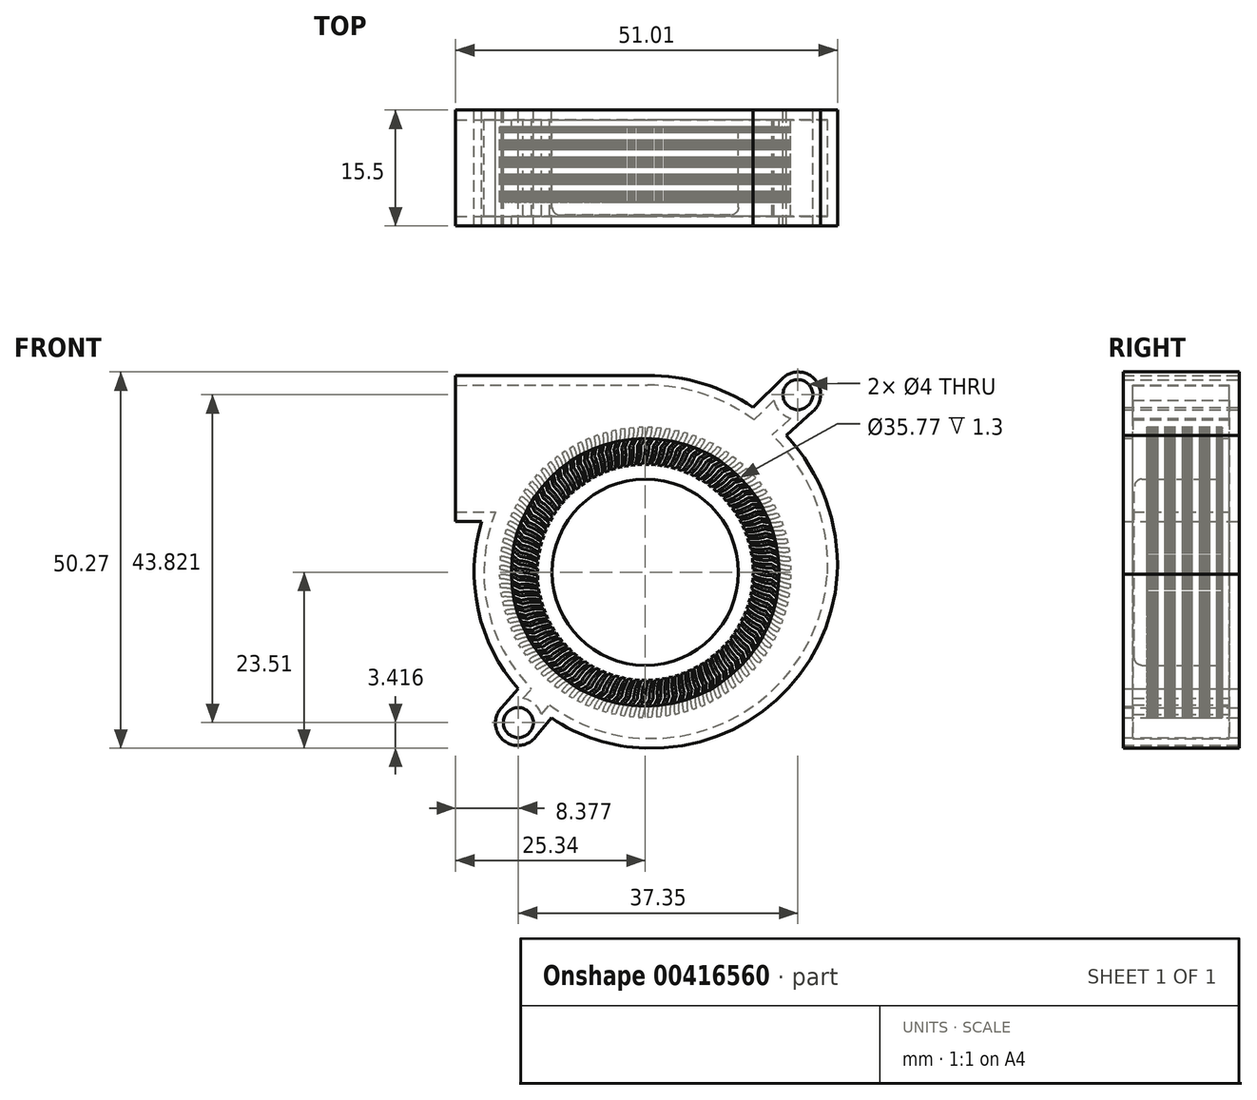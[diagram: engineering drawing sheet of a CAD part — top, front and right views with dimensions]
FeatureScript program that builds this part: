
annotation { "Feature Type Name" : "Feature", "Feature Type Description" : "" }
export const myFeature = defineFeature(function(context is Context, id is Id, definition is map)
    precondition{}
    {
        {
            var Q0;
            Q0=qCreatedBy(makeId("Front.planeOp"),FACE);
            var sketch = newSketch(context, id + "F0", { "sketchPlane" : qUnion([Q0])});
            skCircle(sketch, "E0", {"center": v(0, 0) * mm, "radius": 12.44 * mm});
            skCircle(sketch, "E1", {"center": v(0, 0) * mm, "radius": 15.98 * mm});
            skCircle(sketch, "E2.0", {"center": v(0, 0) * mm, "radius": 17.88 * mm});
            skLineSegment(sketch, "E3", {"start": v(-25.34, 6.78) * mm, "end": v(-25.34, 26.28) * mm});
            skLineSegment(sketch, "E4", {"start": v(-25.34, 6.78) * mm, "end": v(-21.86, 6.78) * mm});
            skLineSegment(sketch, "E5", {"start": v(-25.34, 26.28) * mm, "end": v(0.29, 26.3) * mm});
            skArc(sketch, "E6", {"start": v(25.64, -0.28) * mm, "mid": v(18.67, 18.45) * mm, "end": v(0.29, 26.3) * mm});
            skArc(sketch, "E7", {"start": v(0, -23.5) * mm, "mid": v(17.52, -17.08) * mm, "end": v(25.64, -0.28) * mm});
            skArc(sketch, "E8", {"start": v(-21.86, 6.78) * mm, "mid": v(-18.42, -13.77) * mm, "end": v(0, -23.5) * mm});
            skCircle(sketch, "E9", {"center": v(20.39, 23.73) * mm, "radius": 2 * mm});
            skCircle(sketch, "E10", {"center": v(-16.96, -20.1) * mm, "radius": 2 * mm});
            skLineSegment(sketch, "E11", {"start": v(22.42, 21.52) * mm, "end": v(18.83, 18.28) * mm});
            skLineSegment(sketch, "E12", {"start": v(18.32, 25.9) * mm, "end": v(14.4, 22.03) * mm});
            skArc(sketch, "E13", {"start": v(22.42, 21.52) * mm, "mid": v(22.61, 25.82) * mm, "end": v(18.32, 25.9) * mm});
            skLineSegment(sketch, "E14", {"start": v(-19.2, -18.1) * mm, "end": v(-16.96, -15.6) * mm});
            skLineSegment(sketch, "E15", {"start": v(-14.7, -22.06) * mm, "end": v(-12.56, -19.47) * mm});
            skArc(sketch, "E16", {"start": v(-19.2, -18.1) * mm, "mid": v(-19, -22.4) * mm, "end": v(-14.7, -22.06) * mm});
            skSolve(sketch);
        }
        {
            var Q0;
            Q0=makeQuery(id+"F0.imprint","IMPRINT",FACE,{"disambiguationData":[TD([[makeQuery(id+"F0.imprint","IMPRINT",EDGE,{"derivedFrom":sQuery(id+"F0.wireOp",EDGE,"E2.0")}),-1.0]])]});
            var Q1;
            Q1=makeQuery(id+"F0.imprint","IMPRINT",FACE,{"disambiguationData":[TD([[makeQuery(id+"F0.imprint","IMPRINT",EDGE,{"derivedFrom":sQuery(id+"F0.wireOp",EDGE,"E9")}),-1.0]])]});
            var Q2;
            Q2=makeQuery(id+"F0.imprint","IMPRINT",FACE,{"disambiguationData":[TD([[makeQuery(id+"F0.imprint","IMPRINT",EDGE,{"derivedFrom":sQuery(id+"F0.wireOp",EDGE,"E10")}),-1.0]])]});
            extrude(context, id + "F1", {"entities" : qUnion([Q0, Q1, Q2]), "depth" : 15.5 * mm});
        }
        {
            var Q0;
            Q0=makeQuery(id+"F1.opExtrude","SWEPT_FACE",FACE,{"disambiguationData":[OSD([sQuery(id+"F0.wireOp",EDGE,"E3")])]});
            var Q1;
            Q1=makeQuery(id+"F1.opExtrude","SWEPT_FACE",FACE,{"disambiguationData":[OSD([sQuery(id+"F0.wireOp",EDGE,"E2.0")])]});
            shell(context, id + "F2", {"entities" : qUnion([Q0, Q1]), "thickness" : 1.3 * mm});
        }
        {
            var Q0;
            Q0=makeQuery(id+"F0.imprint","IMPRINT",FACE,{"disambiguationData":[TD([[makeQuery(id+"F0.imprint","IMPRINT",EDGE,{"derivedFrom":sQuery(id+"F0.wireOp",EDGE,"E0")}),-1.0]])]});
            var Q1;
            Q1=makeQuery(id+"F0.imprint","IMPRINT",FACE,{"disambiguationData":[TD([[makeQuery(id+"F0.imprint","IMPRINT",EDGE,{"derivedFrom":sQuery(id+"F0.wireOp",EDGE,"E0")}),1.0]])]});
            extrude(context, id + "F3", {"entities" : qUnion([Q0, Q1]), "operationType" : NewBodyOperationType.ADD, "depth" : 1.3 * mm});
        }
        {
            var Q0;
            Q0=makeQuery(id+"F0.imprint","IMPRINT",FACE,{"disambiguationData":[TD([[makeQuery(id+"F0.imprint","IMPRINT",EDGE,{"derivedFrom":sQuery(id+"F0.wireOp",EDGE,"E1")}),-1.0]])]});
            var Q1;
            Q1=makeQuery(id+"F0.imprint","IMPRINT",FACE,{"disambiguationData":[TD([[makeQuery(id+"F0.imprint","IMPRINT",EDGE,{"derivedFrom":sQuery(id+"F0.wireOp",EDGE,"E0")}),-1.0]])]});
            var Q2;
            Q2=makeQuery(id+"F0.imprint","IMPRINT",FACE,{"disambiguationData":[TD([[makeQuery(id+"F0.imprint","IMPRINT",EDGE,{"derivedFrom":sQuery(id+"F0.wireOp",EDGE,"E0")}),1.0]])]});
            extrude(context, id + "F4", {"entities" : qUnion([Q0, Q1, Q2]), "depth" : 2.3 * mm});
        }
        {
            var Q0;
            Q0=makeQuery(id+"F0.imprint","IMPRINT",FACE,{"disambiguationData":[TD([[makeQuery(id+"F0.imprint","IMPRINT",EDGE,{"derivedFrom":sQuery(id+"F0.wireOp",EDGE,"E0")}),1.0]])]});
            extrude(context, id + "F5", {"entities" : qUnion([Q0]), "operationType" : NewBodyOperationType.ADD, "depth" : 14 * mm});
        }
        {
            var Q0;
            Q0=makeQuery(id+"F5.opExtrude","CAP_FACE",FACE,{"disambiguationData":[OSD([sQuery(id+"F0.wireOp",EDGE,"E0")])],"isStart":false});
            fillet(context, id + "F6", {"entities" : qUnion([Q0]), "radius" : 1 * mm, "tangentPropagation" : true, "allowEdgeOverflow" : false});
        }
        {
            var Q0;
            Q0=makeQuery(id+"F0.imprint","IMPRINT",FACE,{"disambiguationData":[TD([[makeQuery(id+"F0.imprint","IMPRINT",EDGE,{"derivedFrom":sQuery(id+"F0.wireOp",EDGE,"E1")}),-1.0]])]});
            extrude(context, id + "F7", {"entities" : qUnion([Q0]), "operationType" : NewBodyOperationType.ADD, "depth" : 1.3 * mm});
        }
        {
            var Q0;
            Q0=makeQuery(id+"F4.opExtrude","CAP_FACE",FACE,{"disambiguationData":[OSD([sQuery(id+"F0.wireOp",EDGE,"E2.0")])],"isStart":false});
            var sketch = newSketch(context, id + "F8", { "sketchPlane" : qUnion([Q0])});
            skLineSegment(sketch, "E17", {"start": v(-0.45, 14.4) * mm, "end": v(-1.01, 14.4) * mm});
            skLineSegment(sketch, "E18.MirrorCS", {"start": v(0.34, 19.42) * mm, "end": v(0.91, 19.42) * mm});
            skArc(sketch, "E19", {"start": v(-1.01, 14.4) * mm, "mid": v(-0.64, 15.64) * mm, "end": v(-0.6, 16.93) * mm});
            skArc(sketch, "E20", {"start": v(-0.6, 16.93) * mm, "mid": v(0.04, 18.11) * mm, "end": v(0.34, 19.42) * mm});
            skArc(sketch, "E21", {"start": v(0, 16.93) * mm, "mid": v(0.67, 18.1) * mm, "end": v(0.91, 19.42) * mm});
            skArc(sketch, "E22", {"start": v(-0.45, 14.4) * mm, "mid": v(-0.11, 15.65) * mm, "end": v(0, 16.93) * mm});
            skArc(sketch, "E23.1.0", {"start": v(-1.91, 14.31) * mm, "mid": v(-1.62, 15.57) * mm, "end": v(-1.66, 16.86) * mm});
            skArc(sketch, "E23.1.1", {"start": v(-1.66, 16.86) * mm, "mid": v(-1.1, 18.08) * mm, "end": v(-0.87, 19.4) * mm});
            skArc(sketch, "E23.1.2", {"start": v(-1.35, 14.35) * mm, "mid": v(-1.1, 15.61) * mm, "end": v(-1.06, 16.9) * mm});
            skArc(sketch, "E23.1.3", {"start": v(-1.06, 16.9) * mm, "mid": v(-0.47, 18.1) * mm, "end": v(-0.31, 19.44) * mm});
            skLineSegment(sketch, "E23.1.4", {"start": v(-1.35, 14.35) * mm, "end": v(-1.91, 14.31) * mm});
            skLineSegment(sketch, "E23.1.5", {"start": v(-0.87, 19.4) * mm, "end": v(-0.31, 19.44) * mm});
            skArc(sketch, "E23.2.0", {"start": v(-2.8, 14.16) * mm, "mid": v(-2.6, 15.44) * mm, "end": v(-2.71, 16.73) * mm});
            skArc(sketch, "E23.2.1", {"start": v(-2.71, 16.73) * mm, "mid": v(-2.23, 17.97) * mm, "end": v(-2.1, 19.3) * mm});
            skArc(sketch, "E23.2.2", {"start": v(-2.25, 14.23) * mm, "mid": v(-2.07, 15.51) * mm, "end": v(-2.12, 16.8) * mm});
            skArc(sketch, "E23.2.3", {"start": v(-2.12, 16.8) * mm, "mid": v(-1.6, 18.04) * mm, "end": v(-1.53, 19.38) * mm});
            skLineSegment(sketch, "E23.2.4", {"start": v(-2.25, 14.23) * mm, "end": v(-2.8, 14.16) * mm});
            skLineSegment(sketch, "E23.2.5", {"start": v(-2.1, 19.3) * mm, "end": v(-1.53, 19.38) * mm});
            skArc(sketch, "E23.3.0", {"start": v(-3.7, 13.96) * mm, "mid": v(-3.56, 15.24) * mm, "end": v(-3.76, 16.52) * mm});
            skArc(sketch, "E23.3.1", {"start": v(-3.76, 16.52) * mm, "mid": v(-3.35, 17.8) * mm, "end": v(-3.3, 19.14) * mm});
            skArc(sketch, "E23.3.2", {"start": v(-3.14, 14.06) * mm, "mid": v(-3.04, 15.35) * mm, "end": v(-3.17, 16.64) * mm});
            skArc(sketch, "E23.3.3", {"start": v(-3.17, 16.64) * mm, "mid": v(-2.74, 17.9) * mm, "end": v(-2.74, 19.24) * mm});
            skLineSegment(sketch, "E23.3.4", {"start": v(-3.14, 14.06) * mm, "end": v(-3.7, 13.96) * mm});
            skLineSegment(sketch, "E23.3.5", {"start": v(-3.3, 19.14) * mm, "end": v(-2.74, 19.24) * mm});
            skArc(sketch, "E23.4.0", {"start": v(-4.56, 13.7) * mm, "mid": v(-4.5, 15) * mm, "end": v(-4.79, 16.26) * mm});
            skArc(sketch, "E23.4.1", {"start": v(-4.79, 16.26) * mm, "mid": v(-4.46, 17.55) * mm, "end": v(-4.5, 18.9) * mm});
            skArc(sketch, "E23.4.2", {"start": v(-4.01, 13.84) * mm, "mid": v(-4, 15.13) * mm, "end": v(-4.21, 16.4) * mm});
            skArc(sketch, "E23.4.3", {"start": v(-4.21, 16.4) * mm, "mid": v(-3.85, 17.7) * mm, "end": v(-3.95, 19.03) * mm});
            skLineSegment(sketch, "E23.4.4", {"start": v(-4.01, 13.84) * mm, "end": v(-4.56, 13.7) * mm});
            skLineSegment(sketch, "E23.4.5", {"start": v(-4.5, 18.9) * mm, "end": v(-3.95, 19.03) * mm});
            skArc(sketch, "E23.5.0", {"start": v(-5.41, 13.38) * mm, "mid": v(-5.44, 14.68) * mm, "end": v(-5.8, 15.92) * mm});
            skArc(sketch, "E23.5.1", {"start": v(-5.8, 15.92) * mm, "mid": v(-5.56, 17.24) * mm, "end": v(-5.67, 18.57) * mm});
            skArc(sketch, "E23.5.2", {"start": v(-4.87, 13.56) * mm, "mid": v(-4.94, 14.85) * mm, "end": v(-5.23, 16.1) * mm});
            skArc(sketch, "E23.5.3", {"start": v(-5.23, 16.1) * mm, "mid": v(-4.96, 17.42) * mm, "end": v(-5.13, 18.75) * mm});
            skLineSegment(sketch, "E23.5.4", {"start": v(-4.87, 13.56) * mm, "end": v(-5.41, 13.38) * mm});
            skLineSegment(sketch, "E23.5.5", {"start": v(-5.67, 18.57) * mm, "end": v(-5.13, 18.75) * mm});
            skArc(sketch, "E23.6.0", {"start": v(-6.24, 13.02) * mm, "mid": v(-6.35, 14.3) * mm, "end": v(-6.79, 15.53) * mm});
            skArc(sketch, "E23.6.1", {"start": v(-6.79, 15.53) * mm, "mid": v(-6.63, 16.86) * mm, "end": v(-6.83, 18.18) * mm});
            skArc(sketch, "E23.6.2", {"start": v(-5.72, 13.23) * mm, "mid": v(-5.87, 14.5) * mm, "end": v(-6.23, 15.75) * mm});
            skArc(sketch, "E23.6.3", {"start": v(-6.23, 15.75) * mm, "mid": v(-6.04, 17.07) * mm, "end": v(-6.3, 18.39) * mm});
            skLineSegment(sketch, "E23.6.4", {"start": v(-5.72, 13.23) * mm, "end": v(-6.24, 13.02) * mm});
            skLineSegment(sketch, "E23.6.5", {"start": v(-6.83, 18.18) * mm, "end": v(-6.3, 18.39) * mm});
            skArc(sketch, "E23.7.0", {"start": v(-7.05, 12.6) * mm, "mid": v(-7.24, 13.88) * mm, "end": v(-7.75, 15.07) * mm});
            skArc(sketch, "E23.7.1", {"start": v(-7.75, 15.07) * mm, "mid": v(-7.67, 16.4) * mm, "end": v(-7.95, 17.72) * mm});
            skArc(sketch, "E23.7.2", {"start": v(-6.54, 12.84) * mm, "mid": v(-6.76, 14.11) * mm, "end": v(-7.21, 15.32) * mm});
            skArc(sketch, "E23.7.3", {"start": v(-7.21, 15.32) * mm, "mid": v(-7.1, 16.66) * mm, "end": v(-7.44, 17.96) * mm});
            skLineSegment(sketch, "E23.7.4", {"start": v(-6.54, 12.84) * mm, "end": v(-7.05, 12.6) * mm});
            skLineSegment(sketch, "E23.7.5", {"start": v(-7.95, 17.72) * mm, "end": v(-7.44, 17.96) * mm});
            skArc(sketch, "E23.8.0", {"start": v(-7.83, 12.13) * mm, "mid": v(-8.1, 13.4) * mm, "end": v(-8.68, 14.55) * mm});
            skArc(sketch, "E23.8.1", {"start": v(-8.68, 14.55) * mm, "mid": v(-8.69, 15.9) * mm, "end": v(-9.05, 17.18) * mm});
            skArc(sketch, "E23.8.2", {"start": v(-7.33, 12.4) * mm, "mid": v(-7.64, 13.66) * mm, "end": v(-8.16, 14.84) * mm});
            skArc(sketch, "E23.8.3", {"start": v(-8.16, 14.84) * mm, "mid": v(-8.13, 16.18) * mm, "end": v(-8.56, 17.45) * mm});
            skLineSegment(sketch, "E23.8.4", {"start": v(-7.33, 12.4) * mm, "end": v(-7.83, 12.13) * mm});
            skLineSegment(sketch, "E23.8.5", {"start": v(-9.05, 17.18) * mm, "end": v(-8.56, 17.45) * mm});
            skArc(sketch, "E23.9.0", {"start": v(-8.57, 11.62) * mm, "mid": v(-8.92, 12.86) * mm, "end": v(-9.58, 13.98) * mm});
            skArc(sketch, "E23.9.1", {"start": v(-9.58, 13.98) * mm, "mid": v(-9.67, 15.32) * mm, "end": v(-10.11, 16.58) * mm});
            skArc(sketch, "E23.9.2", {"start": v(-8.1, 11.92) * mm, "mid": v(-8.48, 13.15) * mm, "end": v(-9.07, 14.3) * mm});
            skArc(sketch, "E23.9.3", {"start": v(-9.07, 14.3) * mm, "mid": v(-9.13, 15.64) * mm, "end": v(-9.63, 16.88) * mm});
            skLineSegment(sketch, "E23.9.4", {"start": v(-8.1, 11.92) * mm, "end": v(-8.57, 11.62) * mm});
            skLineSegment(sketch, "E23.9.5", {"start": v(-10.11, 16.58) * mm, "end": v(-9.63, 16.88) * mm});
            skArc(sketch, "E23.10.0", {"start": v(-9.28, 11.06) * mm, "mid": v(-9.7, 12.28) * mm, "end": v(-10.43, 13.35) * mm});
            skArc(sketch, "E23.10.1", {"start": v(-10.43, 13.35) * mm, "mid": v(-10.61, 14.68) * mm, "end": v(-11.13, 15.91) * mm});
            skArc(sketch, "E23.10.2", {"start": v(-8.83, 11.39) * mm, "mid": v(-9.29, 12.6) * mm, "end": v(-9.95, 13.7) * mm});
            skArc(sketch, "E23.10.3", {"start": v(-9.95, 13.7) * mm, "mid": v(-10.1, 15.03) * mm, "end": v(-10.68, 16.24) * mm});
            skLineSegment(sketch, "E23.10.4", {"start": v(-8.83, 11.39) * mm, "end": v(-9.28, 11.06) * mm});
            skLineSegment(sketch, "E23.10.5", {"start": v(-11.13, 15.91) * mm, "end": v(-10.68, 16.24) * mm});
            skArc(sketch, "E23.11.0", {"start": v(-9.96, 10.45) * mm, "mid": v(-10.46, 11.65) * mm, "end": v(-11.25, 12.67) * mm});
            skArc(sketch, "E23.11.1", {"start": v(-11.25, 12.67) * mm, "mid": v(-11.51, 13.98) * mm, "end": v(-12.11, 15.18) * mm});
            skArc(sketch, "E23.11.2", {"start": v(-9.52, 10.81) * mm, "mid": v(-10.06, 11.99) * mm, "end": v(-10.8, 13.05) * mm});
            skArc(sketch, "E23.11.3", {"start": v(-10.8, 13.05) * mm, "mid": v(-11.02, 14.37) * mm, "end": v(-11.67, 15.54) * mm});
            skLineSegment(sketch, "E23.11.4", {"start": v(-9.52, 10.81) * mm, "end": v(-9.96, 10.45) * mm});
            skLineSegment(sketch, "E23.11.5", {"start": v(-12.11, 15.18) * mm, "end": v(-11.67, 15.54) * mm});
            skArc(sketch, "E23.12.0", {"start": v(-10.6, 9.8) * mm, "mid": v(-11.17, 10.97) * mm, "end": v(-12.03, 11.94) * mm});
            skArc(sketch, "E23.12.1", {"start": v(-12.03, 11.94) * mm, "mid": v(-12.37, 13.23) * mm, "end": v(-13.04, 14.39) * mm});
            skArc(sketch, "E23.12.2", {"start": v(-10.18, 10.2) * mm, "mid": v(-10.8, 11.33) * mm, "end": v(-11.6, 12.35) * mm});
            skArc(sketch, "E23.12.3", {"start": v(-11.6, 12.35) * mm, "mid": v(-11.9, 13.65) * mm, "end": v(-12.63, 14.78) * mm});
            skLineSegment(sketch, "E23.12.4", {"start": v(-10.18, 10.2) * mm, "end": v(-10.6, 9.8) * mm});
            skLineSegment(sketch, "E23.12.5", {"start": v(-13.04, 14.39) * mm, "end": v(-12.63, 14.78) * mm});
            skArc(sketch, "E23.13.0", {"start": v(-11.2, 9.12) * mm, "mid": v(-11.84, 10.24) * mm, "end": v(-12.75, 11.16) * mm});
            skArc(sketch, "E23.13.1", {"start": v(-12.75, 11.16) * mm, "mid": v(-13.17, 12.43) * mm, "end": v(-13.92, 13.54) * mm});
            skArc(sketch, "E23.13.2", {"start": v(-10.8, 9.53) * mm, "mid": v(-11.48, 10.63) * mm, "end": v(-12.35, 11.6) * mm});
            skArc(sketch, "E23.13.3", {"start": v(-12.35, 11.6) * mm, "mid": v(-12.74, 12.88) * mm, "end": v(-13.53, 13.96) * mm});
            skLineSegment(sketch, "E23.13.4", {"start": v(-10.8, 9.53) * mm, "end": v(-11.2, 9.12) * mm});
            skLineSegment(sketch, "E23.13.5", {"start": v(-13.92, 13.54) * mm, "end": v(-13.53, 13.96) * mm});
            skArc(sketch, "E23.14.0", {"start": v(-11.74, 8.4) * mm, "mid": v(-12.46, 9.48) * mm, "end": v(-13.43, 10.34) * mm});
            skArc(sketch, "E23.14.1", {"start": v(-13.43, 10.34) * mm, "mid": v(-13.93, 11.58) * mm, "end": v(-14.74, 12.64) * mm});
            skArc(sketch, "E23.14.2", {"start": v(-11.38, 8.84) * mm, "mid": v(-12.13, 9.89) * mm, "end": v(-13.05, 10.8) * mm});
            skArc(sketch, "E23.14.3", {"start": v(-13.05, 10.8) * mm, "mid": v(-13.52, 12.05) * mm, "end": v(-14.38, 13.08) * mm});
            skLineSegment(sketch, "E23.14.4", {"start": v(-11.38, 8.84) * mm, "end": v(-11.74, 8.4) * mm});
            skLineSegment(sketch, "E23.14.5", {"start": v(-14.74, 12.64) * mm, "end": v(-14.38, 13.08) * mm});
            skArc(sketch, "E23.15.0", {"start": v(-12.25, 7.65) * mm, "mid": v(-13.03, 8.68) * mm, "end": v(-14.05, 9.47) * mm});
            skArc(sketch, "E23.15.1", {"start": v(-14.05, 9.47) * mm, "mid": v(-14.63, 10.68) * mm, "end": v(-15.5, 11.7) * mm});
            skArc(sketch, "E23.15.2", {"start": v(-11.91, 8.1) * mm, "mid": v(-12.73, 9.1) * mm, "end": v(-13.7, 9.95) * mm});
            skArc(sketch, "E23.15.3", {"start": v(-13.7, 9.95) * mm, "mid": v(-14.25, 11.18) * mm, "end": v(-15.17, 12.15) * mm});
            skLineSegment(sketch, "E23.15.4", {"start": v(-11.91, 8.1) * mm, "end": v(-12.25, 7.65) * mm});
            skLineSegment(sketch, "E23.15.5", {"start": v(-15.5, 11.7) * mm, "end": v(-15.17, 12.15) * mm});
            skArc(sketch, "E23.16.0", {"start": v(-12.7, 6.86) * mm, "mid": v(-13.55, 7.84) * mm, "end": v(-14.62, 8.57) * mm});
            skArc(sketch, "E23.16.1", {"start": v(-14.62, 8.57) * mm, "mid": v(-15.27, 9.74) * mm, "end": v(-16.2, 10.7) * mm});
            skArc(sketch, "E23.16.2", {"start": v(-12.4, 7.34) * mm, "mid": v(-13.27, 8.3) * mm, "end": v(-14.3, 9.07) * mm});
            skArc(sketch, "E23.16.3", {"start": v(-14.3, 9.07) * mm, "mid": v(-14.92, 10.26) * mm, "end": v(-15.9, 11.17) * mm});
            skLineSegment(sketch, "E23.16.4", {"start": v(-12.4, 7.34) * mm, "end": v(-12.7, 6.86) * mm});
            skLineSegment(sketch, "E23.16.5", {"start": v(-16.2, 10.7) * mm, "end": v(-15.9, 11.17) * mm});
            skArc(sketch, "E23.17.0", {"start": v(-13.1, 6.05) * mm, "mid": v(-14.01, 6.98) * mm, "end": v(-15.13, 7.64) * mm});
            skArc(sketch, "E23.17.1", {"start": v(-15.13, 7.64) * mm, "mid": v(-15.85, 8.76) * mm, "end": v(-16.85, 9.66) * mm});
            skArc(sketch, "E23.17.2", {"start": v(-12.84, 6.55) * mm, "mid": v(-13.77, 7.44) * mm, "end": v(-14.84, 8.16) * mm});
            skArc(sketch, "E23.17.3", {"start": v(-14.84, 8.16) * mm, "mid": v(-15.54, 9.3) * mm, "end": v(-16.58, 10.15) * mm});
            skLineSegment(sketch, "E23.17.4", {"start": v(-12.84, 6.55) * mm, "end": v(-13.1, 6.05) * mm});
            skLineSegment(sketch, "E23.17.5", {"start": v(-16.85, 9.66) * mm, "end": v(-16.58, 10.15) * mm});
            skArc(sketch, "E23.18.0", {"start": v(-13.46, 5.22) * mm, "mid": v(-14.42, 6.08) * mm, "end": v(-15.58, 6.67) * mm});
            skArc(sketch, "E23.18.1", {"start": v(-15.58, 6.67) * mm, "mid": v(-16.37, 7.75) * mm, "end": v(-17.42, 8.58) * mm});
            skArc(sketch, "E23.18.2", {"start": v(-13.22, 5.73) * mm, "mid": v(-14.2, 6.56) * mm, "end": v(-15.32, 7.21) * mm});
            skArc(sketch, "E23.18.3", {"start": v(-15.32, 7.21) * mm, "mid": v(-16.1, 8.3) * mm, "end": v(-17.18, 9.1) * mm});
            skLineSegment(sketch, "E23.18.4", {"start": v(-13.22, 5.73) * mm, "end": v(-13.46, 5.22) * mm});
            skLineSegment(sketch, "E23.18.5", {"start": v(-17.42, 8.58) * mm, "end": v(-17.18, 9.1) * mm});
            skArc(sketch, "E23.19.0", {"start": v(-13.76, 4.36) * mm, "mid": v(-14.78, 5.16) * mm, "end": v(-15.96, 5.68) * mm});
            skArc(sketch, "E23.19.1", {"start": v(-15.96, 5.68) * mm, "mid": v(-16.82, 6.7) * mm, "end": v(-17.93, 7.47) * mm});
            skArc(sketch, "E23.19.2", {"start": v(-13.55, 4.89) * mm, "mid": v(-14.6, 5.66) * mm, "end": v(-15.75, 6.23) * mm});
            skArc(sketch, "E23.19.3", {"start": v(-15.75, 6.23) * mm, "mid": v(-16.58, 7.28) * mm, "end": v(-17.72, 8) * mm});
            skLineSegment(sketch, "E23.19.4", {"start": v(-13.55, 4.89) * mm, "end": v(-13.76, 4.36) * mm});
            skLineSegment(sketch, "E23.19.5", {"start": v(-17.93, 7.47) * mm, "end": v(-17.72, 8) * mm});
            skArc(sketch, "E23.20.0", {"start": v(-14, 3.49) * mm, "mid": v(-15.07, 4.23) * mm, "end": v(-16.29, 4.67) * mm});
            skArc(sketch, "E23.20.1", {"start": v(-16.29, 4.67) * mm, "mid": v(-17.21, 5.64) * mm, "end": v(-18.36, 6.33) * mm});
            skArc(sketch, "E23.20.2", {"start": v(-13.84, 4.03) * mm, "mid": v(-14.92, 4.73) * mm, "end": v(-16.1, 5.23) * mm});
            skArc(sketch, "E23.20.3", {"start": v(-16.1, 5.23) * mm, "mid": v(-17, 6.23) * mm, "end": v(-18.18, 6.87) * mm});
            skLineSegment(sketch, "E23.20.4", {"start": v(-13.84, 4.03) * mm, "end": v(-14, 3.49) * mm});
            skLineSegment(sketch, "E23.20.5", {"start": v(-18.36, 6.33) * mm, "end": v(-18.18, 6.87) * mm});
            skArc(sketch, "E23.21.0", {"start": v(-14.2, 2.6) * mm, "mid": v(-15.3, 3.27) * mm, "end": v(-16.55, 3.64) * mm});
            skArc(sketch, "E23.21.1", {"start": v(-16.55, 3.64) * mm, "mid": v(-17.53, 4.55) * mm, "end": v(-18.72, 5.16) * mm});
            skArc(sketch, "E23.21.2", {"start": v(-14.06, 3.15) * mm, "mid": v(-15.19, 3.78) * mm, "end": v(-16.4, 4.21) * mm});
            skArc(sketch, "E23.21.3", {"start": v(-16.4, 4.21) * mm, "mid": v(-17.36, 5.15) * mm, "end": v(-18.58, 5.71) * mm});
            skLineSegment(sketch, "E23.21.4", {"start": v(-14.06, 3.15) * mm, "end": v(-14.2, 2.6) * mm});
            skLineSegment(sketch, "E23.21.5", {"start": v(-18.72, 5.16) * mm, "end": v(-18.58, 5.71) * mm});
            skArc(sketch, "E23.22.0", {"start": v(-14.34, 1.7) * mm, "mid": v(-15.48, 2.3) * mm, "end": v(-16.75, 2.59) * mm});
            skArc(sketch, "E23.22.1", {"start": v(-16.75, 2.59) * mm, "mid": v(-17.78, 3.44) * mm, "end": v(-19, 3.98) * mm});
            skArc(sketch, "E23.22.2", {"start": v(-14.23, 2.26) * mm, "mid": v(-15.4, 2.82) * mm, "end": v(-16.64, 3.17) * mm});
            skArc(sketch, "E23.22.3", {"start": v(-16.64, 3.17) * mm, "mid": v(-17.65, 4.05) * mm, "end": v(-18.9, 4.53) * mm});
            skLineSegment(sketch, "E23.22.4", {"start": v(-14.23, 2.26) * mm, "end": v(-14.34, 1.7) * mm});
            skLineSegment(sketch, "E23.22.5", {"start": v(-19, 3.98) * mm, "end": v(-18.9, 4.53) * mm});
            skArc(sketch, "E23.23.0", {"start": v(-14.42, 0.8) * mm, "mid": v(-15.6, 1.33) * mm, "end": v(-16.88, 1.53) * mm});
            skArc(sketch, "E23.23.1", {"start": v(-16.88, 1.53) * mm, "mid": v(-17.96, 2.31) * mm, "end": v(-19.22, 2.78) * mm});
            skArc(sketch, "E23.23.2", {"start": v(-14.34, 1.36) * mm, "mid": v(-15.54, 1.85) * mm, "end": v(-16.8, 2.12) * mm});
            skArc(sketch, "E23.23.3", {"start": v(-16.8, 2.12) * mm, "mid": v(-17.87, 2.93) * mm, "end": v(-19.15, 3.34) * mm});
            skLineSegment(sketch, "E23.23.4", {"start": v(-14.34, 1.36) * mm, "end": v(-14.42, 0.8) * mm});
            skLineSegment(sketch, "E23.23.5", {"start": v(-19.22, 2.78) * mm, "end": v(-19.15, 3.34) * mm});
            skArc(sketch, "E23.24.0", {"start": v(-14.44, -0.1) * mm, "mid": v(-15.65, 0.35) * mm, "end": v(-16.94, 0.47) * mm});
            skArc(sketch, "E23.24.1", {"start": v(-16.94, 0.47) * mm, "mid": v(-18.07, 1.18) * mm, "end": v(-19.36, 1.56) * mm});
            skArc(sketch, "E23.24.2", {"start": v(-14.4, 0.46) * mm, "mid": v(-15.63, 0.87) * mm, "end": v(-16.9, 1.06) * mm});
            skArc(sketch, "E23.24.3", {"start": v(-16.9, 1.06) * mm, "mid": v(-18.02, 1.8) * mm, "end": v(-19.32, 2.13) * mm});
            skLineSegment(sketch, "E23.24.4", {"start": v(-14.4, 0.46) * mm, "end": v(-14.44, -0.1) * mm});
            skLineSegment(sketch, "E23.24.5", {"start": v(-19.36, 1.56) * mm, "end": v(-19.32, 2.13) * mm});
            skArc(sketch, "E23.25.0", {"start": v(-14.4, -1.01) * mm, "mid": v(-15.64, -0.64) * mm, "end": v(-16.93, -0.6) * mm});
            skArc(sketch, "E23.25.1", {"start": v(-16.93, -0.6) * mm, "mid": v(-18.11, 0.04) * mm, "end": v(-19.42, 0.34) * mm});
            skArc(sketch, "E23.25.2", {"start": v(-14.4, -0.45) * mm, "mid": v(-15.65, -0.11) * mm, "end": v(-16.93, 0) * mm});
            skArc(sketch, "E23.25.3", {"start": v(-16.93, 0) * mm, "mid": v(-18.1, 0.67) * mm, "end": v(-19.42, 0.91) * mm});
            skLineSegment(sketch, "E23.25.4", {"start": v(-14.4, -0.45) * mm, "end": v(-14.4, -1.01) * mm});
            skLineSegment(sketch, "E23.25.5", {"start": v(-19.42, 0.34) * mm, "end": v(-19.42, 0.91) * mm});
            skArc(sketch, "E23.26.0", {"start": v(-14.31, -1.91) * mm, "mid": v(-15.57, -1.62) * mm, "end": v(-16.86, -1.66) * mm});
            skArc(sketch, "E23.26.1", {"start": v(-16.86, -1.66) * mm, "mid": v(-18.08, -1.1) * mm, "end": v(-19.4, -0.87) * mm});
            skArc(sketch, "E23.26.2", {"start": v(-14.35, -1.35) * mm, "mid": v(-15.61, -1.1) * mm, "end": v(-16.9, -1.06) * mm});
            skArc(sketch, "E23.26.3", {"start": v(-16.9, -1.06) * mm, "mid": v(-18.1, -0.47) * mm, "end": v(-19.44, -0.31) * mm});
            skLineSegment(sketch, "E23.26.4", {"start": v(-14.35, -1.35) * mm, "end": v(-14.31, -1.91) * mm});
            skLineSegment(sketch, "E23.26.5", {"start": v(-19.4, -0.87) * mm, "end": v(-19.44, -0.31) * mm});
            skArc(sketch, "E23.27.0", {"start": v(-14.16, -2.8) * mm, "mid": v(-15.44, -2.6) * mm, "end": v(-16.73, -2.71) * mm});
            skArc(sketch, "E23.27.1", {"start": v(-16.73, -2.71) * mm, "mid": v(-17.97, -2.23) * mm, "end": v(-19.3, -2.1) * mm});
            skArc(sketch, "E23.27.2", {"start": v(-14.23, -2.25) * mm, "mid": v(-15.51, -2.07) * mm, "end": v(-16.8, -2.12) * mm});
            skArc(sketch, "E23.27.3", {"start": v(-16.8, -2.12) * mm, "mid": v(-18.04, -1.6) * mm, "end": v(-19.38, -1.53) * mm});
            skLineSegment(sketch, "E23.27.4", {"start": v(-14.23, -2.25) * mm, "end": v(-14.16, -2.8) * mm});
            skLineSegment(sketch, "E23.27.5", {"start": v(-19.3, -2.1) * mm, "end": v(-19.38, -1.53) * mm});
            skArc(sketch, "E23.28.0", {"start": v(-13.96, -3.7) * mm, "mid": v(-15.24, -3.56) * mm, "end": v(-16.52, -3.76) * mm});
            skArc(sketch, "E23.28.1", {"start": v(-16.52, -3.76) * mm, "mid": v(-17.8, -3.35) * mm, "end": v(-19.14, -3.3) * mm});
            skArc(sketch, "E23.28.2", {"start": v(-14.06, -3.14) * mm, "mid": v(-15.35, -3.04) * mm, "end": v(-16.64, -3.17) * mm});
            skArc(sketch, "E23.28.3", {"start": v(-16.64, -3.17) * mm, "mid": v(-17.9, -2.74) * mm, "end": v(-19.24, -2.74) * mm});
            skLineSegment(sketch, "E23.28.4", {"start": v(-14.06, -3.14) * mm, "end": v(-13.96, -3.7) * mm});
            skLineSegment(sketch, "E23.28.5", {"start": v(-19.14, -3.3) * mm, "end": v(-19.24, -2.74) * mm});
            skArc(sketch, "E23.29.0", {"start": v(-13.7, -4.56) * mm, "mid": v(-15, -4.5) * mm, "end": v(-16.26, -4.79) * mm});
            skArc(sketch, "E23.29.1", {"start": v(-16.26, -4.79) * mm, "mid": v(-17.55, -4.46) * mm, "end": v(-18.9, -4.5) * mm});
            skArc(sketch, "E23.29.2", {"start": v(-13.84, -4.01) * mm, "mid": v(-15.13, -4) * mm, "end": v(-16.4, -4.21) * mm});
            skArc(sketch, "E23.29.3", {"start": v(-16.4, -4.21) * mm, "mid": v(-17.7, -3.85) * mm, "end": v(-19.03, -3.95) * mm});
            skLineSegment(sketch, "E23.29.4", {"start": v(-13.84, -4.01) * mm, "end": v(-13.7, -4.56) * mm});
            skLineSegment(sketch, "E23.29.5", {"start": v(-18.9, -4.5) * mm, "end": v(-19.03, -3.95) * mm});
            skArc(sketch, "E23.30.0", {"start": v(-13.38, -5.41) * mm, "mid": v(-14.68, -5.44) * mm, "end": v(-15.92, -5.8) * mm});
            skArc(sketch, "E23.30.1", {"start": v(-15.92, -5.8) * mm, "mid": v(-17.24, -5.56) * mm, "end": v(-18.57, -5.67) * mm});
            skArc(sketch, "E23.30.2", {"start": v(-13.56, -4.87) * mm, "mid": v(-14.85, -4.94) * mm, "end": v(-16.1, -5.23) * mm});
            skArc(sketch, "E23.30.3", {"start": v(-16.1, -5.23) * mm, "mid": v(-17.42, -4.96) * mm, "end": v(-18.75, -5.13) * mm});
            skLineSegment(sketch, "E23.30.4", {"start": v(-13.56, -4.87) * mm, "end": v(-13.38, -5.41) * mm});
            skLineSegment(sketch, "E23.30.5", {"start": v(-18.57, -5.67) * mm, "end": v(-18.75, -5.13) * mm});
            skArc(sketch, "E23.31.0", {"start": v(-13.02, -6.24) * mm, "mid": v(-14.3, -6.35) * mm, "end": v(-15.53, -6.79) * mm});
            skArc(sketch, "E23.31.1", {"start": v(-15.53, -6.79) * mm, "mid": v(-16.86, -6.63) * mm, "end": v(-18.18, -6.83) * mm});
            skArc(sketch, "E23.31.2", {"start": v(-13.23, -5.72) * mm, "mid": v(-14.5, -5.87) * mm, "end": v(-15.75, -6.23) * mm});
            skArc(sketch, "E23.31.3", {"start": v(-15.75, -6.23) * mm, "mid": v(-17.07, -6.04) * mm, "end": v(-18.39, -6.3) * mm});
            skLineSegment(sketch, "E23.31.4", {"start": v(-13.23, -5.72) * mm, "end": v(-13.02, -6.24) * mm});
            skLineSegment(sketch, "E23.31.5", {"start": v(-18.18, -6.83) * mm, "end": v(-18.39, -6.3) * mm});
            skArc(sketch, "E23.32.0", {"start": v(-12.6, -7.05) * mm, "mid": v(-13.88, -7.24) * mm, "end": v(-15.07, -7.75) * mm});
            skArc(sketch, "E23.32.1", {"start": v(-15.07, -7.75) * mm, "mid": v(-16.4, -7.67) * mm, "end": v(-17.72, -7.95) * mm});
            skArc(sketch, "E23.32.2", {"start": v(-12.84, -6.54) * mm, "mid": v(-14.11, -6.76) * mm, "end": v(-15.32, -7.21) * mm});
            skArc(sketch, "E23.32.3", {"start": v(-15.32, -7.21) * mm, "mid": v(-16.66, -7.1) * mm, "end": v(-17.96, -7.44) * mm});
            skLineSegment(sketch, "E23.32.4", {"start": v(-12.84, -6.54) * mm, "end": v(-12.6, -7.05) * mm});
            skLineSegment(sketch, "E23.32.5", {"start": v(-17.72, -7.95) * mm, "end": v(-17.96, -7.44) * mm});
            skArc(sketch, "E23.33.0", {"start": v(-12.13, -7.83) * mm, "mid": v(-13.4, -8.1) * mm, "end": v(-14.55, -8.68) * mm});
            skArc(sketch, "E23.33.1", {"start": v(-14.55, -8.68) * mm, "mid": v(-15.9, -8.69) * mm, "end": v(-17.18, -9.05) * mm});
            skArc(sketch, "E23.33.2", {"start": v(-12.4, -7.33) * mm, "mid": v(-13.66, -7.64) * mm, "end": v(-14.84, -8.16) * mm});
            skArc(sketch, "E23.33.3", {"start": v(-14.84, -8.16) * mm, "mid": v(-16.18, -8.13) * mm, "end": v(-17.45, -8.56) * mm});
            skLineSegment(sketch, "E23.33.4", {"start": v(-12.4, -7.33) * mm, "end": v(-12.13, -7.83) * mm});
            skLineSegment(sketch, "E23.33.5", {"start": v(-17.18, -9.05) * mm, "end": v(-17.45, -8.56) * mm});
            skArc(sketch, "E23.34.0", {"start": v(-11.62, -8.57) * mm, "mid": v(-12.86, -8.92) * mm, "end": v(-13.98, -9.58) * mm});
            skArc(sketch, "E23.34.1", {"start": v(-13.98, -9.58) * mm, "mid": v(-15.32, -9.67) * mm, "end": v(-16.58, -10.11) * mm});
            skArc(sketch, "E23.34.2", {"start": v(-11.92, -8.1) * mm, "mid": v(-13.15, -8.48) * mm, "end": v(-14.3, -9.07) * mm});
            skArc(sketch, "E23.34.3", {"start": v(-14.3, -9.07) * mm, "mid": v(-15.64, -9.13) * mm, "end": v(-16.88, -9.63) * mm});
            skLineSegment(sketch, "E23.34.4", {"start": v(-11.92, -8.1) * mm, "end": v(-11.62, -8.57) * mm});
            skLineSegment(sketch, "E23.34.5", {"start": v(-16.58, -10.11) * mm, "end": v(-16.88, -9.63) * mm});
            skArc(sketch, "E23.35.0", {"start": v(-11.06, -9.28) * mm, "mid": v(-12.28, -9.7) * mm, "end": v(-13.35, -10.43) * mm});
            skArc(sketch, "E23.35.1", {"start": v(-13.35, -10.43) * mm, "mid": v(-14.68, -10.61) * mm, "end": v(-15.91, -11.13) * mm});
            skArc(sketch, "E23.35.2", {"start": v(-11.39, -8.83) * mm, "mid": v(-12.6, -9.29) * mm, "end": v(-13.7, -9.95) * mm});
            skArc(sketch, "E23.35.3", {"start": v(-13.7, -9.95) * mm, "mid": v(-15.03, -10.1) * mm, "end": v(-16.24, -10.68) * mm});
            skLineSegment(sketch, "E23.35.4", {"start": v(-11.39, -8.83) * mm, "end": v(-11.06, -9.28) * mm});
            skLineSegment(sketch, "E23.35.5", {"start": v(-15.91, -11.13) * mm, "end": v(-16.24, -10.68) * mm});
            skArc(sketch, "E23.36.0", {"start": v(-10.45, -9.96) * mm, "mid": v(-11.65, -10.46) * mm, "end": v(-12.67, -11.25) * mm});
            skArc(sketch, "E23.36.1", {"start": v(-12.67, -11.25) * mm, "mid": v(-13.98, -11.51) * mm, "end": v(-15.18, -12.11) * mm});
            skArc(sketch, "E23.36.2", {"start": v(-10.81, -9.52) * mm, "mid": v(-11.99, -10.06) * mm, "end": v(-13.05, -10.8) * mm});
            skArc(sketch, "E23.36.3", {"start": v(-13.05, -10.8) * mm, "mid": v(-14.37, -11.02) * mm, "end": v(-15.54, -11.67) * mm});
            skLineSegment(sketch, "E23.36.4", {"start": v(-10.81, -9.52) * mm, "end": v(-10.45, -9.96) * mm});
            skLineSegment(sketch, "E23.36.5", {"start": v(-15.18, -12.11) * mm, "end": v(-15.54, -11.67) * mm});
            skArc(sketch, "E23.37.0", {"start": v(-9.8, -10.6) * mm, "mid": v(-10.97, -11.17) * mm, "end": v(-11.94, -12.03) * mm});
            skArc(sketch, "E23.37.1", {"start": v(-11.94, -12.03) * mm, "mid": v(-13.23, -12.37) * mm, "end": v(-14.39, -13.04) * mm});
            skArc(sketch, "E23.37.2", {"start": v(-10.2, -10.18) * mm, "mid": v(-11.33, -10.8) * mm, "end": v(-12.35, -11.6) * mm});
            skArc(sketch, "E23.37.3", {"start": v(-12.35, -11.6) * mm, "mid": v(-13.65, -11.9) * mm, "end": v(-14.78, -12.63) * mm});
            skLineSegment(sketch, "E23.37.4", {"start": v(-10.2, -10.18) * mm, "end": v(-9.8, -10.6) * mm});
            skLineSegment(sketch, "E23.37.5", {"start": v(-14.39, -13.04) * mm, "end": v(-14.78, -12.63) * mm});
            skArc(sketch, "E23.38.0", {"start": v(-9.12, -11.2) * mm, "mid": v(-10.24, -11.84) * mm, "end": v(-11.16, -12.75) * mm});
            skArc(sketch, "E23.38.1", {"start": v(-11.16, -12.75) * mm, "mid": v(-12.43, -13.17) * mm, "end": v(-13.54, -13.92) * mm});
            skArc(sketch, "E23.38.2", {"start": v(-9.53, -10.8) * mm, "mid": v(-10.63, -11.48) * mm, "end": v(-11.6, -12.35) * mm});
            skArc(sketch, "E23.38.3", {"start": v(-11.6, -12.35) * mm, "mid": v(-12.88, -12.74) * mm, "end": v(-13.96, -13.53) * mm});
            skLineSegment(sketch, "E23.38.4", {"start": v(-9.53, -10.8) * mm, "end": v(-9.12, -11.2) * mm});
            skLineSegment(sketch, "E23.38.5", {"start": v(-13.54, -13.92) * mm, "end": v(-13.96, -13.53) * mm});
            skArc(sketch, "E23.39.0", {"start": v(-8.4, -11.74) * mm, "mid": v(-9.48, -12.46) * mm, "end": v(-10.34, -13.43) * mm});
            skArc(sketch, "E23.39.1", {"start": v(-10.34, -13.43) * mm, "mid": v(-11.58, -13.93) * mm, "end": v(-12.64, -14.74) * mm});
            skArc(sketch, "E23.39.2", {"start": v(-8.84, -11.38) * mm, "mid": v(-9.89, -12.13) * mm, "end": v(-10.8, -13.05) * mm});
            skArc(sketch, "E23.39.3", {"start": v(-10.8, -13.05) * mm, "mid": v(-12.05, -13.52) * mm, "end": v(-13.08, -14.38) * mm});
            skLineSegment(sketch, "E23.39.4", {"start": v(-8.84, -11.38) * mm, "end": v(-8.4, -11.74) * mm});
            skLineSegment(sketch, "E23.39.5", {"start": v(-12.64, -14.74) * mm, "end": v(-13.08, -14.38) * mm});
            skArc(sketch, "E23.40.0", {"start": v(-7.65, -12.25) * mm, "mid": v(-8.68, -13.03) * mm, "end": v(-9.47, -14.05) * mm});
            skArc(sketch, "E23.40.1", {"start": v(-9.47, -14.05) * mm, "mid": v(-10.68, -14.63) * mm, "end": v(-11.7, -15.5) * mm});
            skArc(sketch, "E23.40.2", {"start": v(-8.1, -11.91) * mm, "mid": v(-9.1, -12.73) * mm, "end": v(-9.95, -13.7) * mm});
            skArc(sketch, "E23.40.3", {"start": v(-9.95, -13.7) * mm, "mid": v(-11.18, -14.25) * mm, "end": v(-12.15, -15.17) * mm});
            skLineSegment(sketch, "E23.40.4", {"start": v(-8.1, -11.91) * mm, "end": v(-7.65, -12.25) * mm});
            skLineSegment(sketch, "E23.40.5", {"start": v(-11.7, -15.5) * mm, "end": v(-12.15, -15.17) * mm});
            skArc(sketch, "E23.41.0", {"start": v(-6.86, -12.7) * mm, "mid": v(-7.84, -13.55) * mm, "end": v(-8.57, -14.62) * mm});
            skArc(sketch, "E23.41.1", {"start": v(-8.57, -14.62) * mm, "mid": v(-9.74, -15.27) * mm, "end": v(-10.7, -16.2) * mm});
            skArc(sketch, "E23.41.2", {"start": v(-7.34, -12.4) * mm, "mid": v(-8.3, -13.27) * mm, "end": v(-9.07, -14.3) * mm});
            skArc(sketch, "E23.41.3", {"start": v(-9.07, -14.3) * mm, "mid": v(-10.26, -14.92) * mm, "end": v(-11.17, -15.9) * mm});
            skLineSegment(sketch, "E23.41.4", {"start": v(-7.34, -12.4) * mm, "end": v(-6.86, -12.7) * mm});
            skLineSegment(sketch, "E23.41.5", {"start": v(-10.7, -16.2) * mm, "end": v(-11.17, -15.9) * mm});
            skArc(sketch, "E23.42.0", {"start": v(-6.05, -13.1) * mm, "mid": v(-6.98, -14.01) * mm, "end": v(-7.64, -15.13) * mm});
            skArc(sketch, "E23.42.1", {"start": v(-7.64, -15.13) * mm, "mid": v(-8.76, -15.85) * mm, "end": v(-9.66, -16.85) * mm});
            skArc(sketch, "E23.42.2", {"start": v(-6.55, -12.84) * mm, "mid": v(-7.44, -13.77) * mm, "end": v(-8.16, -14.84) * mm});
            skArc(sketch, "E23.42.3", {"start": v(-8.16, -14.84) * mm, "mid": v(-9.3, -15.54) * mm, "end": v(-10.15, -16.58) * mm});
            skLineSegment(sketch, "E23.42.4", {"start": v(-6.55, -12.84) * mm, "end": v(-6.05, -13.1) * mm});
            skLineSegment(sketch, "E23.42.5", {"start": v(-9.66, -16.85) * mm, "end": v(-10.15, -16.58) * mm});
            skArc(sketch, "E23.43.0", {"start": v(-5.22, -13.46) * mm, "mid": v(-6.08, -14.42) * mm, "end": v(-6.67, -15.58) * mm});
            skArc(sketch, "E23.43.1", {"start": v(-6.67, -15.58) * mm, "mid": v(-7.75, -16.37) * mm, "end": v(-8.58, -17.42) * mm});
            skArc(sketch, "E23.43.2", {"start": v(-5.73, -13.22) * mm, "mid": v(-6.56, -14.2) * mm, "end": v(-7.21, -15.32) * mm});
            skArc(sketch, "E23.43.3", {"start": v(-7.21, -15.32) * mm, "mid": v(-8.3, -16.1) * mm, "end": v(-9.1, -17.18) * mm});
            skLineSegment(sketch, "E23.43.4", {"start": v(-5.73, -13.22) * mm, "end": v(-5.22, -13.46) * mm});
            skLineSegment(sketch, "E23.43.5", {"start": v(-8.58, -17.42) * mm, "end": v(-9.1, -17.18) * mm});
            skArc(sketch, "E23.44.0", {"start": v(-4.36, -13.76) * mm, "mid": v(-5.16, -14.78) * mm, "end": v(-5.68, -15.96) * mm});
            skArc(sketch, "E23.44.1", {"start": v(-5.68, -15.96) * mm, "mid": v(-6.7, -16.82) * mm, "end": v(-7.47, -17.93) * mm});
            skArc(sketch, "E23.44.2", {"start": v(-4.89, -13.55) * mm, "mid": v(-5.66, -14.6) * mm, "end": v(-6.23, -15.75) * mm});
            skArc(sketch, "E23.44.3", {"start": v(-6.23, -15.75) * mm, "mid": v(-7.28, -16.58) * mm, "end": v(-8, -17.72) * mm});
            skLineSegment(sketch, "E23.44.4", {"start": v(-4.89, -13.55) * mm, "end": v(-4.36, -13.76) * mm});
            skLineSegment(sketch, "E23.44.5", {"start": v(-7.47, -17.93) * mm, "end": v(-8, -17.72) * mm});
            skArc(sketch, "E23.45.0", {"start": v(-3.49, -14) * mm, "mid": v(-4.23, -15.07) * mm, "end": v(-4.67, -16.29) * mm});
            skArc(sketch, "E23.45.1", {"start": v(-4.67, -16.29) * mm, "mid": v(-5.64, -17.21) * mm, "end": v(-6.33, -18.36) * mm});
            skArc(sketch, "E23.45.2", {"start": v(-4.03, -13.84) * mm, "mid": v(-4.73, -14.92) * mm, "end": v(-5.23, -16.1) * mm});
            skArc(sketch, "E23.45.3", {"start": v(-5.23, -16.1) * mm, "mid": v(-6.23, -17) * mm, "end": v(-6.87, -18.18) * mm});
            skLineSegment(sketch, "E23.45.4", {"start": v(-4.03, -13.84) * mm, "end": v(-3.49, -14) * mm});
            skLineSegment(sketch, "E23.45.5", {"start": v(-6.33, -18.36) * mm, "end": v(-6.87, -18.18) * mm});
            skArc(sketch, "E23.46.0", {"start": v(-2.6, -14.2) * mm, "mid": v(-3.27, -15.3) * mm, "end": v(-3.64, -16.55) * mm});
            skArc(sketch, "E23.46.1", {"start": v(-3.64, -16.55) * mm, "mid": v(-4.55, -17.53) * mm, "end": v(-5.16, -18.72) * mm});
            skArc(sketch, "E23.46.2", {"start": v(-3.15, -14.06) * mm, "mid": v(-3.78, -15.19) * mm, "end": v(-4.21, -16.4) * mm});
            skArc(sketch, "E23.46.3", {"start": v(-4.21, -16.4) * mm, "mid": v(-5.15, -17.36) * mm, "end": v(-5.71, -18.58) * mm});
            skLineSegment(sketch, "E23.46.4", {"start": v(-3.15, -14.06) * mm, "end": v(-2.6, -14.2) * mm});
            skLineSegment(sketch, "E23.46.5", {"start": v(-5.16, -18.72) * mm, "end": v(-5.71, -18.58) * mm});
            skArc(sketch, "E23.47.0", {"start": v(-1.7, -14.34) * mm, "mid": v(-2.3, -15.48) * mm, "end": v(-2.59, -16.75) * mm});
            skArc(sketch, "E23.47.1", {"start": v(-2.59, -16.75) * mm, "mid": v(-3.44, -17.78) * mm, "end": v(-3.98, -19) * mm});
            skArc(sketch, "E23.47.2", {"start": v(-2.26, -14.23) * mm, "mid": v(-2.82, -15.4) * mm, "end": v(-3.17, -16.64) * mm});
            skArc(sketch, "E23.47.3", {"start": v(-3.17, -16.64) * mm, "mid": v(-4.05, -17.65) * mm, "end": v(-4.53, -18.9) * mm});
            skLineSegment(sketch, "E23.47.4", {"start": v(-2.26, -14.23) * mm, "end": v(-1.7, -14.34) * mm});
            skLineSegment(sketch, "E23.47.5", {"start": v(-3.98, -19) * mm, "end": v(-4.53, -18.9) * mm});
            skArc(sketch, "E23.48.0", {"start": v(-0.8, -14.42) * mm, "mid": v(-1.33, -15.6) * mm, "end": v(-1.53, -16.88) * mm});
            skArc(sketch, "E23.48.1", {"start": v(-1.53, -16.88) * mm, "mid": v(-2.31, -17.96) * mm, "end": v(-2.78, -19.22) * mm});
            skArc(sketch, "E23.48.2", {"start": v(-1.36, -14.34) * mm, "mid": v(-1.85, -15.54) * mm, "end": v(-2.12, -16.8) * mm});
            skArc(sketch, "E23.48.3", {"start": v(-2.12, -16.8) * mm, "mid": v(-2.93, -17.87) * mm, "end": v(-3.34, -19.15) * mm});
            skLineSegment(sketch, "E23.48.4", {"start": v(-1.36, -14.34) * mm, "end": v(-0.8, -14.42) * mm});
            skLineSegment(sketch, "E23.48.5", {"start": v(-2.78, -19.22) * mm, "end": v(-3.34, -19.15) * mm});
            skArc(sketch, "E23.49.0", {"start": v(0.1, -14.44) * mm, "mid": v(-0.35, -15.65) * mm, "end": v(-0.47, -16.94) * mm});
            skArc(sketch, "E23.49.1", {"start": v(-0.47, -16.94) * mm, "mid": v(-1.18, -18.07) * mm, "end": v(-1.56, -19.36) * mm});
            skArc(sketch, "E23.49.2", {"start": v(-0.46, -14.4) * mm, "mid": v(-0.87, -15.63) * mm, "end": v(-1.06, -16.9) * mm});
            skArc(sketch, "E23.49.3", {"start": v(-1.06, -16.9) * mm, "mid": v(-1.8, -18.02) * mm, "end": v(-2.13, -19.32) * mm});
            skLineSegment(sketch, "E23.49.4", {"start": v(-0.46, -14.4) * mm, "end": v(0.1, -14.44) * mm});
            skLineSegment(sketch, "E23.49.5", {"start": v(-1.56, -19.36) * mm, "end": v(-2.13, -19.32) * mm});
            skArc(sketch, "E23.50.0", {"start": v(1.01, -14.4) * mm, "mid": v(0.64, -15.64) * mm, "end": v(0.6, -16.93) * mm});
            skArc(sketch, "E23.50.1", {"start": v(0.6, -16.93) * mm, "mid": v(-0.04, -18.11) * mm, "end": v(-0.34, -19.42) * mm});
            skArc(sketch, "E23.50.2", {"start": v(0.45, -14.4) * mm, "mid": v(0.11, -15.65) * mm, "end": v(0, -16.93) * mm});
            skArc(sketch, "E23.50.3", {"start": v(0, -16.93) * mm, "mid": v(-0.67, -18.1) * mm, "end": v(-0.91, -19.42) * mm});
            skLineSegment(sketch, "E23.50.4", {"start": v(0.45, -14.4) * mm, "end": v(1.01, -14.4) * mm});
            skLineSegment(sketch, "E23.50.5", {"start": v(-0.34, -19.42) * mm, "end": v(-0.91, -19.42) * mm});
            skArc(sketch, "E23.51.0", {"start": v(1.91, -14.31) * mm, "mid": v(1.62, -15.57) * mm, "end": v(1.66, -16.86) * mm});
            skArc(sketch, "E23.51.1", {"start": v(1.66, -16.86) * mm, "mid": v(1.1, -18.08) * mm, "end": v(0.87, -19.4) * mm});
            skArc(sketch, "E23.51.2", {"start": v(1.35, -14.35) * mm, "mid": v(1.1, -15.61) * mm, "end": v(1.06, -16.9) * mm});
            skArc(sketch, "E23.51.3", {"start": v(1.06, -16.9) * mm, "mid": v(0.47, -18.1) * mm, "end": v(0.31, -19.44) * mm});
            skLineSegment(sketch, "E23.51.4", {"start": v(1.35, -14.35) * mm, "end": v(1.91, -14.31) * mm});
            skLineSegment(sketch, "E23.51.5", {"start": v(0.87, -19.4) * mm, "end": v(0.31, -19.44) * mm});
            skArc(sketch, "E23.52.0", {"start": v(2.8, -14.16) * mm, "mid": v(2.6, -15.44) * mm, "end": v(2.71, -16.73) * mm});
            skArc(sketch, "E23.52.1", {"start": v(2.71, -16.73) * mm, "mid": v(2.23, -17.97) * mm, "end": v(2.1, -19.3) * mm});
            skArc(sketch, "E23.52.2", {"start": v(2.25, -14.23) * mm, "mid": v(2.07, -15.51) * mm, "end": v(2.12, -16.8) * mm});
            skArc(sketch, "E23.52.3", {"start": v(2.12, -16.8) * mm, "mid": v(1.6, -18.04) * mm, "end": v(1.53, -19.38) * mm});
            skLineSegment(sketch, "E23.52.4", {"start": v(2.25, -14.23) * mm, "end": v(2.8, -14.16) * mm});
            skLineSegment(sketch, "E23.52.5", {"start": v(2.1, -19.3) * mm, "end": v(1.53, -19.38) * mm});
            skArc(sketch, "E23.53.0", {"start": v(3.7, -13.96) * mm, "mid": v(3.56, -15.24) * mm, "end": v(3.76, -16.52) * mm});
            skArc(sketch, "E23.53.1", {"start": v(3.76, -16.52) * mm, "mid": v(3.35, -17.8) * mm, "end": v(3.3, -19.14) * mm});
            skArc(sketch, "E23.53.2", {"start": v(3.14, -14.06) * mm, "mid": v(3.04, -15.35) * mm, "end": v(3.17, -16.64) * mm});
            skArc(sketch, "E23.53.3", {"start": v(3.17, -16.64) * mm, "mid": v(2.74, -17.9) * mm, "end": v(2.74, -19.24) * mm});
            skLineSegment(sketch, "E23.53.4", {"start": v(3.14, -14.06) * mm, "end": v(3.7, -13.96) * mm});
            skLineSegment(sketch, "E23.53.5", {"start": v(3.3, -19.14) * mm, "end": v(2.74, -19.24) * mm});
            skArc(sketch, "E23.54.0", {"start": v(4.56, -13.7) * mm, "mid": v(4.5, -15) * mm, "end": v(4.79, -16.26) * mm});
            skArc(sketch, "E23.54.1", {"start": v(4.79, -16.26) * mm, "mid": v(4.46, -17.55) * mm, "end": v(4.5, -18.9) * mm});
            skArc(sketch, "E23.54.2", {"start": v(4.01, -13.84) * mm, "mid": v(4, -15.13) * mm, "end": v(4.21, -16.4) * mm});
            skArc(sketch, "E23.54.3", {"start": v(4.21, -16.4) * mm, "mid": v(3.85, -17.7) * mm, "end": v(3.95, -19.03) * mm});
            skLineSegment(sketch, "E23.54.4", {"start": v(4.01, -13.84) * mm, "end": v(4.56, -13.7) * mm});
            skLineSegment(sketch, "E23.54.5", {"start": v(4.5, -18.9) * mm, "end": v(3.95, -19.03) * mm});
            skArc(sketch, "E23.55.0", {"start": v(5.41, -13.38) * mm, "mid": v(5.44, -14.68) * mm, "end": v(5.8, -15.92) * mm});
            skArc(sketch, "E23.55.1", {"start": v(5.8, -15.92) * mm, "mid": v(5.56, -17.24) * mm, "end": v(5.67, -18.57) * mm});
            skArc(sketch, "E23.55.2", {"start": v(4.87, -13.56) * mm, "mid": v(4.94, -14.85) * mm, "end": v(5.23, -16.1) * mm});
            skArc(sketch, "E23.55.3", {"start": v(5.23, -16.1) * mm, "mid": v(4.96, -17.42) * mm, "end": v(5.13, -18.75) * mm});
            skLineSegment(sketch, "E23.55.4", {"start": v(4.87, -13.56) * mm, "end": v(5.41, -13.38) * mm});
            skLineSegment(sketch, "E23.55.5", {"start": v(5.67, -18.57) * mm, "end": v(5.13, -18.75) * mm});
            skArc(sketch, "E23.56.0", {"start": v(6.24, -13.02) * mm, "mid": v(6.35, -14.3) * mm, "end": v(6.79, -15.53) * mm});
            skArc(sketch, "E23.56.1", {"start": v(6.79, -15.53) * mm, "mid": v(6.63, -16.86) * mm, "end": v(6.83, -18.18) * mm});
            skArc(sketch, "E23.56.2", {"start": v(5.72, -13.23) * mm, "mid": v(5.87, -14.5) * mm, "end": v(6.23, -15.75) * mm});
            skArc(sketch, "E23.56.3", {"start": v(6.23, -15.75) * mm, "mid": v(6.04, -17.07) * mm, "end": v(6.3, -18.39) * mm});
            skLineSegment(sketch, "E23.56.4", {"start": v(5.72, -13.23) * mm, "end": v(6.24, -13.02) * mm});
            skLineSegment(sketch, "E23.56.5", {"start": v(6.83, -18.18) * mm, "end": v(6.3, -18.39) * mm});
            skArc(sketch, "E23.57.0", {"start": v(7.05, -12.6) * mm, "mid": v(7.24, -13.88) * mm, "end": v(7.75, -15.07) * mm});
            skArc(sketch, "E23.57.1", {"start": v(7.75, -15.07) * mm, "mid": v(7.67, -16.4) * mm, "end": v(7.95, -17.72) * mm});
            skArc(sketch, "E23.57.2", {"start": v(6.54, -12.84) * mm, "mid": v(6.76, -14.11) * mm, "end": v(7.21, -15.32) * mm});
            skArc(sketch, "E23.57.3", {"start": v(7.21, -15.32) * mm, "mid": v(7.1, -16.66) * mm, "end": v(7.44, -17.96) * mm});
            skLineSegment(sketch, "E23.57.4", {"start": v(6.54, -12.84) * mm, "end": v(7.05, -12.6) * mm});
            skLineSegment(sketch, "E23.57.5", {"start": v(7.95, -17.72) * mm, "end": v(7.44, -17.96) * mm});
            skArc(sketch, "E23.58.0", {"start": v(7.83, -12.13) * mm, "mid": v(8.1, -13.4) * mm, "end": v(8.68, -14.55) * mm});
            skArc(sketch, "E23.58.1", {"start": v(8.68, -14.55) * mm, "mid": v(8.69, -15.9) * mm, "end": v(9.05, -17.18) * mm});
            skArc(sketch, "E23.58.2", {"start": v(7.33, -12.4) * mm, "mid": v(7.64, -13.66) * mm, "end": v(8.16, -14.84) * mm});
            skArc(sketch, "E23.58.3", {"start": v(8.16, -14.84) * mm, "mid": v(8.13, -16.18) * mm, "end": v(8.56, -17.45) * mm});
            skLineSegment(sketch, "E23.58.4", {"start": v(7.33, -12.4) * mm, "end": v(7.83, -12.13) * mm});
            skLineSegment(sketch, "E23.58.5", {"start": v(9.05, -17.18) * mm, "end": v(8.56, -17.45) * mm});
            skArc(sketch, "E23.59.0", {"start": v(8.57, -11.62) * mm, "mid": v(8.92, -12.86) * mm, "end": v(9.58, -13.98) * mm});
            skArc(sketch, "E23.59.1", {"start": v(9.58, -13.98) * mm, "mid": v(9.67, -15.32) * mm, "end": v(10.11, -16.58) * mm});
            skArc(sketch, "E23.59.2", {"start": v(8.1, -11.92) * mm, "mid": v(8.48, -13.15) * mm, "end": v(9.07, -14.3) * mm});
            skArc(sketch, "E23.59.3", {"start": v(9.07, -14.3) * mm, "mid": v(9.13, -15.64) * mm, "end": v(9.63, -16.88) * mm});
            skLineSegment(sketch, "E23.59.4", {"start": v(8.1, -11.92) * mm, "end": v(8.57, -11.62) * mm});
            skLineSegment(sketch, "E23.59.5", {"start": v(10.11, -16.58) * mm, "end": v(9.63, -16.88) * mm});
            skArc(sketch, "E23.60.0", {"start": v(9.28, -11.06) * mm, "mid": v(9.7, -12.28) * mm, "end": v(10.43, -13.35) * mm});
            skArc(sketch, "E23.60.1", {"start": v(10.43, -13.35) * mm, "mid": v(10.61, -14.68) * mm, "end": v(11.13, -15.91) * mm});
            skArc(sketch, "E23.60.2", {"start": v(8.83, -11.39) * mm, "mid": v(9.29, -12.6) * mm, "end": v(9.95, -13.7) * mm});
            skArc(sketch, "E23.60.3", {"start": v(9.95, -13.7) * mm, "mid": v(10.1, -15.03) * mm, "end": v(10.68, -16.24) * mm});
            skLineSegment(sketch, "E23.60.4", {"start": v(8.83, -11.39) * mm, "end": v(9.28, -11.06) * mm});
            skLineSegment(sketch, "E23.60.5", {"start": v(11.13, -15.91) * mm, "end": v(10.68, -16.24) * mm});
            skArc(sketch, "E23.61.0", {"start": v(9.96, -10.45) * mm, "mid": v(10.46, -11.65) * mm, "end": v(11.25, -12.67) * mm});
            skArc(sketch, "E23.61.1", {"start": v(11.25, -12.67) * mm, "mid": v(11.51, -13.98) * mm, "end": v(12.11, -15.18) * mm});
            skArc(sketch, "E23.61.2", {"start": v(9.52, -10.81) * mm, "mid": v(10.06, -11.99) * mm, "end": v(10.8, -13.05) * mm});
            skArc(sketch, "E23.61.3", {"start": v(10.8, -13.05) * mm, "mid": v(11.02, -14.37) * mm, "end": v(11.67, -15.54) * mm});
            skLineSegment(sketch, "E23.61.4", {"start": v(9.52, -10.81) * mm, "end": v(9.96, -10.45) * mm});
            skLineSegment(sketch, "E23.61.5", {"start": v(12.11, -15.18) * mm, "end": v(11.67, -15.54) * mm});
            skArc(sketch, "E23.62.0", {"start": v(10.6, -9.8) * mm, "mid": v(11.17, -10.97) * mm, "end": v(12.03, -11.94) * mm});
            skArc(sketch, "E23.62.1", {"start": v(12.03, -11.94) * mm, "mid": v(12.37, -13.23) * mm, "end": v(13.04, -14.39) * mm});
            skArc(sketch, "E23.62.2", {"start": v(10.18, -10.2) * mm, "mid": v(10.8, -11.33) * mm, "end": v(11.6, -12.35) * mm});
            skArc(sketch, "E23.62.3", {"start": v(11.6, -12.35) * mm, "mid": v(11.9, -13.65) * mm, "end": v(12.63, -14.78) * mm});
            skLineSegment(sketch, "E23.62.4", {"start": v(10.18, -10.2) * mm, "end": v(10.6, -9.8) * mm});
            skLineSegment(sketch, "E23.62.5", {"start": v(13.04, -14.39) * mm, "end": v(12.63, -14.78) * mm});
            skArc(sketch, "E23.63.0", {"start": v(11.2, -9.12) * mm, "mid": v(11.84, -10.24) * mm, "end": v(12.75, -11.16) * mm});
            skArc(sketch, "E23.63.1", {"start": v(12.75, -11.16) * mm, "mid": v(13.17, -12.43) * mm, "end": v(13.92, -13.54) * mm});
            skArc(sketch, "E23.63.2", {"start": v(10.8, -9.53) * mm, "mid": v(11.48, -10.63) * mm, "end": v(12.35, -11.6) * mm});
            skArc(sketch, "E23.63.3", {"start": v(12.35, -11.6) * mm, "mid": v(12.74, -12.88) * mm, "end": v(13.53, -13.96) * mm});
            skLineSegment(sketch, "E23.63.4", {"start": v(10.8, -9.53) * mm, "end": v(11.2, -9.12) * mm});
            skLineSegment(sketch, "E23.63.5", {"start": v(13.92, -13.54) * mm, "end": v(13.53, -13.96) * mm});
            skArc(sketch, "E23.64.0", {"start": v(11.74, -8.4) * mm, "mid": v(12.46, -9.48) * mm, "end": v(13.43, -10.34) * mm});
            skArc(sketch, "E23.64.1", {"start": v(13.43, -10.34) * mm, "mid": v(13.93, -11.58) * mm, "end": v(14.74, -12.64) * mm});
            skArc(sketch, "E23.64.2", {"start": v(11.38, -8.84) * mm, "mid": v(12.13, -9.89) * mm, "end": v(13.05, -10.8) * mm});
            skArc(sketch, "E23.64.3", {"start": v(13.05, -10.8) * mm, "mid": v(13.52, -12.05) * mm, "end": v(14.38, -13.08) * mm});
            skLineSegment(sketch, "E23.64.4", {"start": v(11.38, -8.84) * mm, "end": v(11.74, -8.4) * mm});
            skLineSegment(sketch, "E23.64.5", {"start": v(14.74, -12.64) * mm, "end": v(14.38, -13.08) * mm});
            skArc(sketch, "E23.65.0", {"start": v(12.25, -7.65) * mm, "mid": v(13.03, -8.68) * mm, "end": v(14.05, -9.47) * mm});
            skArc(sketch, "E23.65.1", {"start": v(14.05, -9.47) * mm, "mid": v(14.63, -10.68) * mm, "end": v(15.5, -11.7) * mm});
            skArc(sketch, "E23.65.2", {"start": v(11.91, -8.1) * mm, "mid": v(12.73, -9.1) * mm, "end": v(13.7, -9.95) * mm});
            skArc(sketch, "E23.65.3", {"start": v(13.7, -9.95) * mm, "mid": v(14.25, -11.18) * mm, "end": v(15.17, -12.15) * mm});
            skLineSegment(sketch, "E23.65.4", {"start": v(11.91, -8.1) * mm, "end": v(12.25, -7.65) * mm});
            skLineSegment(sketch, "E23.65.5", {"start": v(15.5, -11.7) * mm, "end": v(15.17, -12.15) * mm});
            skArc(sketch, "E23.66.0", {"start": v(12.7, -6.86) * mm, "mid": v(13.55, -7.84) * mm, "end": v(14.62, -8.57) * mm});
            skArc(sketch, "E23.66.1", {"start": v(14.62, -8.57) * mm, "mid": v(15.27, -9.74) * mm, "end": v(16.2, -10.7) * mm});
            skArc(sketch, "E23.66.2", {"start": v(12.4, -7.34) * mm, "mid": v(13.27, -8.3) * mm, "end": v(14.3, -9.07) * mm});
            skArc(sketch, "E23.66.3", {"start": v(14.3, -9.07) * mm, "mid": v(14.92, -10.26) * mm, "end": v(15.9, -11.17) * mm});
            skLineSegment(sketch, "E23.66.4", {"start": v(12.4, -7.34) * mm, "end": v(12.7, -6.86) * mm});
            skLineSegment(sketch, "E23.66.5", {"start": v(16.2, -10.7) * mm, "end": v(15.9, -11.17) * mm});
            skArc(sketch, "E23.67.0", {"start": v(13.1, -6.05) * mm, "mid": v(14.01, -6.98) * mm, "end": v(15.13, -7.64) * mm});
            skArc(sketch, "E23.67.1", {"start": v(15.13, -7.64) * mm, "mid": v(15.85, -8.76) * mm, "end": v(16.85, -9.66) * mm});
            skArc(sketch, "E23.67.2", {"start": v(12.84, -6.55) * mm, "mid": v(13.77, -7.44) * mm, "end": v(14.84, -8.16) * mm});
            skArc(sketch, "E23.67.3", {"start": v(14.84, -8.16) * mm, "mid": v(15.54, -9.3) * mm, "end": v(16.58, -10.15) * mm});
            skLineSegment(sketch, "E23.67.4", {"start": v(12.84, -6.55) * mm, "end": v(13.1, -6.05) * mm});
            skLineSegment(sketch, "E23.67.5", {"start": v(16.85, -9.66) * mm, "end": v(16.58, -10.15) * mm});
            skArc(sketch, "E23.68.0", {"start": v(13.46, -5.22) * mm, "mid": v(14.42, -6.08) * mm, "end": v(15.58, -6.67) * mm});
            skArc(sketch, "E23.68.1", {"start": v(15.58, -6.67) * mm, "mid": v(16.37, -7.75) * mm, "end": v(17.42, -8.58) * mm});
            skArc(sketch, "E23.68.2", {"start": v(13.22, -5.73) * mm, "mid": v(14.2, -6.56) * mm, "end": v(15.32, -7.21) * mm});
            skArc(sketch, "E23.68.3", {"start": v(15.32, -7.21) * mm, "mid": v(16.1, -8.3) * mm, "end": v(17.18, -9.1) * mm});
            skLineSegment(sketch, "E23.68.4", {"start": v(13.22, -5.73) * mm, "end": v(13.46, -5.22) * mm});
            skLineSegment(sketch, "E23.68.5", {"start": v(17.42, -8.58) * mm, "end": v(17.18, -9.1) * mm});
            skArc(sketch, "E23.69.0", {"start": v(13.76, -4.36) * mm, "mid": v(14.78, -5.16) * mm, "end": v(15.96, -5.68) * mm});
            skArc(sketch, "E23.69.1", {"start": v(15.96, -5.68) * mm, "mid": v(16.82, -6.7) * mm, "end": v(17.93, -7.47) * mm});
            skArc(sketch, "E23.69.2", {"start": v(13.55, -4.89) * mm, "mid": v(14.6, -5.66) * mm, "end": v(15.75, -6.23) * mm});
            skArc(sketch, "E23.69.3", {"start": v(15.75, -6.23) * mm, "mid": v(16.58, -7.28) * mm, "end": v(17.72, -8) * mm});
            skLineSegment(sketch, "E23.69.4", {"start": v(13.55, -4.89) * mm, "end": v(13.76, -4.36) * mm});
            skLineSegment(sketch, "E23.69.5", {"start": v(17.93, -7.47) * mm, "end": v(17.72, -8) * mm});
            skArc(sketch, "E23.70.0", {"start": v(14, -3.49) * mm, "mid": v(15.07, -4.23) * mm, "end": v(16.29, -4.67) * mm});
            skArc(sketch, "E23.70.1", {"start": v(16.29, -4.67) * mm, "mid": v(17.21, -5.64) * mm, "end": v(18.36, -6.33) * mm});
            skArc(sketch, "E23.70.2", {"start": v(13.84, -4.03) * mm, "mid": v(14.92, -4.73) * mm, "end": v(16.1, -5.23) * mm});
            skArc(sketch, "E23.70.3", {"start": v(16.1, -5.23) * mm, "mid": v(17, -6.23) * mm, "end": v(18.18, -6.87) * mm});
            skLineSegment(sketch, "E23.70.4", {"start": v(13.84, -4.03) * mm, "end": v(14, -3.49) * mm});
            skLineSegment(sketch, "E23.70.5", {"start": v(18.36, -6.33) * mm, "end": v(18.18, -6.87) * mm});
            skArc(sketch, "E23.71.0", {"start": v(14.2, -2.6) * mm, "mid": v(15.3, -3.27) * mm, "end": v(16.55, -3.64) * mm});
            skArc(sketch, "E23.71.1", {"start": v(16.55, -3.64) * mm, "mid": v(17.53, -4.55) * mm, "end": v(18.72, -5.16) * mm});
            skArc(sketch, "E23.71.2", {"start": v(14.06, -3.15) * mm, "mid": v(15.19, -3.78) * mm, "end": v(16.4, -4.21) * mm});
            skArc(sketch, "E23.71.3", {"start": v(16.4, -4.21) * mm, "mid": v(17.36, -5.15) * mm, "end": v(18.58, -5.71) * mm});
            skLineSegment(sketch, "E23.71.4", {"start": v(14.06, -3.15) * mm, "end": v(14.2, -2.6) * mm});
            skLineSegment(sketch, "E23.71.5", {"start": v(18.72, -5.16) * mm, "end": v(18.58, -5.71) * mm});
            skArc(sketch, "E23.72.0", {"start": v(14.34, -1.7) * mm, "mid": v(15.48, -2.3) * mm, "end": v(16.75, -2.59) * mm});
            skArc(sketch, "E23.72.1", {"start": v(16.75, -2.59) * mm, "mid": v(17.78, -3.44) * mm, "end": v(19, -3.98) * mm});
            skArc(sketch, "E23.72.2", {"start": v(14.23, -2.26) * mm, "mid": v(15.4, -2.82) * mm, "end": v(16.64, -3.17) * mm});
            skArc(sketch, "E23.72.3", {"start": v(16.64, -3.17) * mm, "mid": v(17.65, -4.05) * mm, "end": v(18.9, -4.53) * mm});
            skLineSegment(sketch, "E23.72.4", {"start": v(14.23, -2.26) * mm, "end": v(14.34, -1.7) * mm});
            skLineSegment(sketch, "E23.72.5", {"start": v(19, -3.98) * mm, "end": v(18.9, -4.53) * mm});
            skArc(sketch, "E23.73.0", {"start": v(14.42, -0.8) * mm, "mid": v(15.6, -1.33) * mm, "end": v(16.88, -1.53) * mm});
            skArc(sketch, "E23.73.1", {"start": v(16.88, -1.53) * mm, "mid": v(17.96, -2.31) * mm, "end": v(19.22, -2.78) * mm});
            skArc(sketch, "E23.73.2", {"start": v(14.34, -1.36) * mm, "mid": v(15.54, -1.85) * mm, "end": v(16.8, -2.12) * mm});
            skArc(sketch, "E23.73.3", {"start": v(16.8, -2.12) * mm, "mid": v(17.87, -2.93) * mm, "end": v(19.15, -3.34) * mm});
            skLineSegment(sketch, "E23.73.4", {"start": v(14.34, -1.36) * mm, "end": v(14.42, -0.8) * mm});
            skLineSegment(sketch, "E23.73.5", {"start": v(19.22, -2.78) * mm, "end": v(19.15, -3.34) * mm});
            skArc(sketch, "E23.74.0", {"start": v(14.44, 0.1) * mm, "mid": v(15.65, -0.35) * mm, "end": v(16.94, -0.47) * mm});
            skArc(sketch, "E23.74.1", {"start": v(16.94, -0.47) * mm, "mid": v(18.07, -1.18) * mm, "end": v(19.36, -1.56) * mm});
            skArc(sketch, "E23.74.2", {"start": v(14.4, -0.46) * mm, "mid": v(15.63, -0.87) * mm, "end": v(16.9, -1.06) * mm});
            skArc(sketch, "E23.74.3", {"start": v(16.9, -1.06) * mm, "mid": v(18.02, -1.8) * mm, "end": v(19.32, -2.13) * mm});
            skLineSegment(sketch, "E23.74.4", {"start": v(14.4, -0.46) * mm, "end": v(14.44, 0.1) * mm});
            skLineSegment(sketch, "E23.74.5", {"start": v(19.36, -1.56) * mm, "end": v(19.32, -2.13) * mm});
            skArc(sketch, "E23.75.0", {"start": v(14.4, 1.01) * mm, "mid": v(15.64, 0.64) * mm, "end": v(16.93, 0.6) * mm});
            skArc(sketch, "E23.75.1", {"start": v(16.93, 0.6) * mm, "mid": v(18.11, -0.04) * mm, "end": v(19.42, -0.34) * mm});
            skArc(sketch, "E23.75.2", {"start": v(14.4, 0.45) * mm, "mid": v(15.65, 0.11) * mm, "end": v(16.93, 0) * mm});
            skArc(sketch, "E23.75.3", {"start": v(16.93, 0) * mm, "mid": v(18.1, -0.67) * mm, "end": v(19.42, -0.91) * mm});
            skLineSegment(sketch, "E23.75.4", {"start": v(14.4, 0.45) * mm, "end": v(14.4, 1.01) * mm});
            skLineSegment(sketch, "E23.75.5", {"start": v(19.42, -0.34) * mm, "end": v(19.42, -0.91) * mm});
            skArc(sketch, "E23.76.0", {"start": v(14.31, 1.91) * mm, "mid": v(15.57, 1.62) * mm, "end": v(16.86, 1.66) * mm});
            skArc(sketch, "E23.76.1", {"start": v(16.86, 1.66) * mm, "mid": v(18.08, 1.1) * mm, "end": v(19.4, 0.87) * mm});
            skArc(sketch, "E23.76.2", {"start": v(14.35, 1.35) * mm, "mid": v(15.61, 1.1) * mm, "end": v(16.9, 1.06) * mm});
            skArc(sketch, "E23.76.3", {"start": v(16.9, 1.06) * mm, "mid": v(18.1, 0.47) * mm, "end": v(19.44, 0.31) * mm});
            skLineSegment(sketch, "E23.76.4", {"start": v(14.35, 1.35) * mm, "end": v(14.31, 1.91) * mm});
            skLineSegment(sketch, "E23.76.5", {"start": v(19.4, 0.87) * mm, "end": v(19.44, 0.31) * mm});
            skArc(sketch, "E23.77.0", {"start": v(14.16, 2.8) * mm, "mid": v(15.44, 2.6) * mm, "end": v(16.73, 2.71) * mm});
            skArc(sketch, "E23.77.1", {"start": v(16.73, 2.71) * mm, "mid": v(17.97, 2.23) * mm, "end": v(19.3, 2.1) * mm});
            skArc(sketch, "E23.77.2", {"start": v(14.23, 2.25) * mm, "mid": v(15.51, 2.07) * mm, "end": v(16.8, 2.12) * mm});
            skArc(sketch, "E23.77.3", {"start": v(16.8, 2.12) * mm, "mid": v(18.04, 1.6) * mm, "end": v(19.38, 1.53) * mm});
            skLineSegment(sketch, "E23.77.4", {"start": v(14.23, 2.25) * mm, "end": v(14.16, 2.8) * mm});
            skLineSegment(sketch, "E23.77.5", {"start": v(19.3, 2.1) * mm, "end": v(19.38, 1.53) * mm});
            skArc(sketch, "E23.78.0", {"start": v(13.96, 3.7) * mm, "mid": v(15.24, 3.56) * mm, "end": v(16.52, 3.76) * mm});
            skArc(sketch, "E23.78.1", {"start": v(16.52, 3.76) * mm, "mid": v(17.8, 3.35) * mm, "end": v(19.14, 3.3) * mm});
            skArc(sketch, "E23.78.2", {"start": v(14.06, 3.14) * mm, "mid": v(15.35, 3.04) * mm, "end": v(16.64, 3.17) * mm});
            skArc(sketch, "E23.78.3", {"start": v(16.64, 3.17) * mm, "mid": v(17.9, 2.74) * mm, "end": v(19.24, 2.74) * mm});
            skLineSegment(sketch, "E23.78.4", {"start": v(14.06, 3.14) * mm, "end": v(13.96, 3.7) * mm});
            skLineSegment(sketch, "E23.78.5", {"start": v(19.14, 3.3) * mm, "end": v(19.24, 2.74) * mm});
            skArc(sketch, "E23.79.0", {"start": v(13.7, 4.56) * mm, "mid": v(15, 4.5) * mm, "end": v(16.26, 4.79) * mm});
            skArc(sketch, "E23.79.1", {"start": v(16.26, 4.79) * mm, "mid": v(17.55, 4.46) * mm, "end": v(18.9, 4.5) * mm});
            skArc(sketch, "E23.79.2", {"start": v(13.84, 4.01) * mm, "mid": v(15.13, 4) * mm, "end": v(16.4, 4.21) * mm});
            skArc(sketch, "E23.79.3", {"start": v(16.4, 4.21) * mm, "mid": v(17.7, 3.85) * mm, "end": v(19.03, 3.95) * mm});
            skLineSegment(sketch, "E23.79.4", {"start": v(13.84, 4.01) * mm, "end": v(13.7, 4.56) * mm});
            skLineSegment(sketch, "E23.79.5", {"start": v(18.9, 4.5) * mm, "end": v(19.03, 3.95) * mm});
            skArc(sketch, "E23.80.0", {"start": v(13.38, 5.41) * mm, "mid": v(14.68, 5.44) * mm, "end": v(15.92, 5.8) * mm});
            skArc(sketch, "E23.80.1", {"start": v(15.92, 5.8) * mm, "mid": v(17.24, 5.56) * mm, "end": v(18.57, 5.67) * mm});
            skArc(sketch, "E23.80.2", {"start": v(13.56, 4.87) * mm, "mid": v(14.85, 4.94) * mm, "end": v(16.1, 5.23) * mm});
            skArc(sketch, "E23.80.3", {"start": v(16.1, 5.23) * mm, "mid": v(17.42, 4.96) * mm, "end": v(18.75, 5.13) * mm});
            skLineSegment(sketch, "E23.80.4", {"start": v(13.56, 4.87) * mm, "end": v(13.38, 5.41) * mm});
            skLineSegment(sketch, "E23.80.5", {"start": v(18.57, 5.67) * mm, "end": v(18.75, 5.13) * mm});
            skArc(sketch, "E23.81.0", {"start": v(13.02, 6.24) * mm, "mid": v(14.3, 6.35) * mm, "end": v(15.53, 6.79) * mm});
            skArc(sketch, "E23.81.1", {"start": v(15.53, 6.79) * mm, "mid": v(16.86, 6.63) * mm, "end": v(18.18, 6.83) * mm});
            skArc(sketch, "E23.81.2", {"start": v(13.23, 5.72) * mm, "mid": v(14.5, 5.87) * mm, "end": v(15.75, 6.23) * mm});
            skArc(sketch, "E23.81.3", {"start": v(15.75, 6.23) * mm, "mid": v(17.07, 6.04) * mm, "end": v(18.39, 6.3) * mm});
            skLineSegment(sketch, "E23.81.4", {"start": v(13.23, 5.72) * mm, "end": v(13.02, 6.24) * mm});
            skLineSegment(sketch, "E23.81.5", {"start": v(18.18, 6.83) * mm, "end": v(18.39, 6.3) * mm});
            skArc(sketch, "E23.82.0", {"start": v(12.6, 7.05) * mm, "mid": v(13.88, 7.24) * mm, "end": v(15.07, 7.75) * mm});
            skArc(sketch, "E23.82.1", {"start": v(15.07, 7.75) * mm, "mid": v(16.4, 7.67) * mm, "end": v(17.72, 7.95) * mm});
            skArc(sketch, "E23.82.2", {"start": v(12.84, 6.54) * mm, "mid": v(14.11, 6.76) * mm, "end": v(15.32, 7.21) * mm});
            skArc(sketch, "E23.82.3", {"start": v(15.32, 7.21) * mm, "mid": v(16.66, 7.1) * mm, "end": v(17.96, 7.44) * mm});
            skLineSegment(sketch, "E23.82.4", {"start": v(12.84, 6.54) * mm, "end": v(12.6, 7.05) * mm});
            skLineSegment(sketch, "E23.82.5", {"start": v(17.72, 7.95) * mm, "end": v(17.96, 7.44) * mm});
            skArc(sketch, "E23.83.0", {"start": v(12.13, 7.83) * mm, "mid": v(13.4, 8.1) * mm, "end": v(14.55, 8.68) * mm});
            skArc(sketch, "E23.83.1", {"start": v(14.55, 8.68) * mm, "mid": v(15.9, 8.69) * mm, "end": v(17.18, 9.05) * mm});
            skArc(sketch, "E23.83.2", {"start": v(12.4, 7.33) * mm, "mid": v(13.66, 7.64) * mm, "end": v(14.84, 8.16) * mm});
            skArc(sketch, "E23.83.3", {"start": v(14.84, 8.16) * mm, "mid": v(16.18, 8.13) * mm, "end": v(17.45, 8.56) * mm});
            skLineSegment(sketch, "E23.83.4", {"start": v(12.4, 7.33) * mm, "end": v(12.13, 7.83) * mm});
            skLineSegment(sketch, "E23.83.5", {"start": v(17.18, 9.05) * mm, "end": v(17.45, 8.56) * mm});
            skArc(sketch, "E23.84.0", {"start": v(11.62, 8.57) * mm, "mid": v(12.86, 8.92) * mm, "end": v(13.98, 9.58) * mm});
            skArc(sketch, "E23.84.1", {"start": v(13.98, 9.58) * mm, "mid": v(15.32, 9.67) * mm, "end": v(16.58, 10.11) * mm});
            skArc(sketch, "E23.84.2", {"start": v(11.92, 8.1) * mm, "mid": v(13.15, 8.48) * mm, "end": v(14.3, 9.07) * mm});
            skArc(sketch, "E23.84.3", {"start": v(14.3, 9.07) * mm, "mid": v(15.64, 9.13) * mm, "end": v(16.88, 9.63) * mm});
            skLineSegment(sketch, "E23.84.4", {"start": v(11.92, 8.1) * mm, "end": v(11.62, 8.57) * mm});
            skLineSegment(sketch, "E23.84.5", {"start": v(16.58, 10.11) * mm, "end": v(16.88, 9.63) * mm});
            skArc(sketch, "E23.85.0", {"start": v(11.06, 9.28) * mm, "mid": v(12.28, 9.7) * mm, "end": v(13.35, 10.43) * mm});
            skArc(sketch, "E23.85.1", {"start": v(13.35, 10.43) * mm, "mid": v(14.68, 10.61) * mm, "end": v(15.91, 11.13) * mm});
            skArc(sketch, "E23.85.2", {"start": v(11.39, 8.83) * mm, "mid": v(12.6, 9.29) * mm, "end": v(13.7, 9.95) * mm});
            skArc(sketch, "E23.85.3", {"start": v(13.7, 9.95) * mm, "mid": v(15.03, 10.1) * mm, "end": v(16.24, 10.68) * mm});
            skLineSegment(sketch, "E23.85.4", {"start": v(11.39, 8.83) * mm, "end": v(11.06, 9.28) * mm});
            skLineSegment(sketch, "E23.85.5", {"start": v(15.91, 11.13) * mm, "end": v(16.24, 10.68) * mm});
            skArc(sketch, "E23.86.0", {"start": v(10.45, 9.96) * mm, "mid": v(11.65, 10.46) * mm, "end": v(12.67, 11.25) * mm});
            skArc(sketch, "E23.86.1", {"start": v(12.67, 11.25) * mm, "mid": v(13.98, 11.51) * mm, "end": v(15.18, 12.11) * mm});
            skArc(sketch, "E23.86.2", {"start": v(10.81, 9.52) * mm, "mid": v(11.99, 10.06) * mm, "end": v(13.05, 10.8) * mm});
            skArc(sketch, "E23.86.3", {"start": v(13.05, 10.8) * mm, "mid": v(14.37, 11.02) * mm, "end": v(15.54, 11.67) * mm});
            skLineSegment(sketch, "E23.86.4", {"start": v(10.81, 9.52) * mm, "end": v(10.45, 9.96) * mm});
            skLineSegment(sketch, "E23.86.5", {"start": v(15.18, 12.11) * mm, "end": v(15.54, 11.67) * mm});
            skArc(sketch, "E23.87.0", {"start": v(9.8, 10.6) * mm, "mid": v(10.97, 11.17) * mm, "end": v(11.94, 12.03) * mm});
            skArc(sketch, "E23.87.1", {"start": v(11.94, 12.03) * mm, "mid": v(13.23, 12.37) * mm, "end": v(14.39, 13.04) * mm});
            skArc(sketch, "E23.87.2", {"start": v(10.2, 10.18) * mm, "mid": v(11.33, 10.8) * mm, "end": v(12.35, 11.6) * mm});
            skArc(sketch, "E23.87.3", {"start": v(12.35, 11.6) * mm, "mid": v(13.65, 11.9) * mm, "end": v(14.78, 12.63) * mm});
            skLineSegment(sketch, "E23.87.4", {"start": v(10.2, 10.18) * mm, "end": v(9.8, 10.6) * mm});
            skLineSegment(sketch, "E23.87.5", {"start": v(14.39, 13.04) * mm, "end": v(14.78, 12.63) * mm});
            skArc(sketch, "E23.88.0", {"start": v(9.12, 11.2) * mm, "mid": v(10.24, 11.84) * mm, "end": v(11.16, 12.75) * mm});
            skArc(sketch, "E23.88.1", {"start": v(11.16, 12.75) * mm, "mid": v(12.43, 13.17) * mm, "end": v(13.54, 13.92) * mm});
            skArc(sketch, "E23.88.2", {"start": v(9.53, 10.8) * mm, "mid": v(10.63, 11.48) * mm, "end": v(11.6, 12.35) * mm});
            skArc(sketch, "E23.88.3", {"start": v(11.6, 12.35) * mm, "mid": v(12.88, 12.74) * mm, "end": v(13.96, 13.53) * mm});
            skLineSegment(sketch, "E23.88.4", {"start": v(9.53, 10.8) * mm, "end": v(9.12, 11.2) * mm});
            skLineSegment(sketch, "E23.88.5", {"start": v(13.54, 13.92) * mm, "end": v(13.96, 13.53) * mm});
            skArc(sketch, "E23.89.0", {"start": v(8.4, 11.74) * mm, "mid": v(9.48, 12.46) * mm, "end": v(10.34, 13.43) * mm});
            skArc(sketch, "E23.89.1", {"start": v(10.34, 13.43) * mm, "mid": v(11.58, 13.93) * mm, "end": v(12.64, 14.74) * mm});
            skArc(sketch, "E23.89.2", {"start": v(8.84, 11.38) * mm, "mid": v(9.89, 12.13) * mm, "end": v(10.8, 13.05) * mm});
            skArc(sketch, "E23.89.3", {"start": v(10.8, 13.05) * mm, "mid": v(12.05, 13.52) * mm, "end": v(13.08, 14.38) * mm});
            skLineSegment(sketch, "E23.89.4", {"start": v(8.84, 11.38) * mm, "end": v(8.4, 11.74) * mm});
            skLineSegment(sketch, "E23.89.5", {"start": v(12.64, 14.74) * mm, "end": v(13.08, 14.38) * mm});
            skArc(sketch, "E23.90.0", {"start": v(7.65, 12.25) * mm, "mid": v(8.68, 13.03) * mm, "end": v(9.47, 14.05) * mm});
            skArc(sketch, "E23.90.1", {"start": v(9.47, 14.05) * mm, "mid": v(10.68, 14.63) * mm, "end": v(11.7, 15.5) * mm});
            skArc(sketch, "E23.90.2", {"start": v(8.1, 11.91) * mm, "mid": v(9.1, 12.73) * mm, "end": v(9.95, 13.7) * mm});
            skArc(sketch, "E23.90.3", {"start": v(9.95, 13.7) * mm, "mid": v(11.18, 14.25) * mm, "end": v(12.15, 15.17) * mm});
            skLineSegment(sketch, "E23.90.4", {"start": v(8.1, 11.91) * mm, "end": v(7.65, 12.25) * mm});
            skLineSegment(sketch, "E23.90.5", {"start": v(11.7, 15.5) * mm, "end": v(12.15, 15.17) * mm});
            skArc(sketch, "E23.91.0", {"start": v(6.86, 12.7) * mm, "mid": v(7.84, 13.55) * mm, "end": v(8.57, 14.62) * mm});
            skArc(sketch, "E23.91.1", {"start": v(8.57, 14.62) * mm, "mid": v(9.74, 15.27) * mm, "end": v(10.7, 16.2) * mm});
            skArc(sketch, "E23.91.2", {"start": v(7.34, 12.4) * mm, "mid": v(8.3, 13.27) * mm, "end": v(9.07, 14.3) * mm});
            skArc(sketch, "E23.91.3", {"start": v(9.07, 14.3) * mm, "mid": v(10.26, 14.92) * mm, "end": v(11.17, 15.9) * mm});
            skLineSegment(sketch, "E23.91.4", {"start": v(7.34, 12.4) * mm, "end": v(6.86, 12.7) * mm});
            skLineSegment(sketch, "E23.91.5", {"start": v(10.7, 16.2) * mm, "end": v(11.17, 15.9) * mm});
            skArc(sketch, "E23.92.0", {"start": v(6.05, 13.1) * mm, "mid": v(6.98, 14.01) * mm, "end": v(7.64, 15.13) * mm});
            skArc(sketch, "E23.92.1", {"start": v(7.64, 15.13) * mm, "mid": v(8.76, 15.85) * mm, "end": v(9.66, 16.85) * mm});
            skArc(sketch, "E23.92.2", {"start": v(6.55, 12.84) * mm, "mid": v(7.44, 13.77) * mm, "end": v(8.16, 14.84) * mm});
            skArc(sketch, "E23.92.3", {"start": v(8.16, 14.84) * mm, "mid": v(9.3, 15.54) * mm, "end": v(10.15, 16.58) * mm});
            skLineSegment(sketch, "E23.92.4", {"start": v(6.55, 12.84) * mm, "end": v(6.05, 13.1) * mm});
            skLineSegment(sketch, "E23.92.5", {"start": v(9.66, 16.85) * mm, "end": v(10.15, 16.58) * mm});
            skArc(sketch, "E23.93.0", {"start": v(5.22, 13.46) * mm, "mid": v(6.08, 14.42) * mm, "end": v(6.67, 15.58) * mm});
            skArc(sketch, "E23.93.1", {"start": v(6.67, 15.58) * mm, "mid": v(7.75, 16.37) * mm, "end": v(8.58, 17.42) * mm});
            skArc(sketch, "E23.93.2", {"start": v(5.73, 13.22) * mm, "mid": v(6.56, 14.2) * mm, "end": v(7.21, 15.32) * mm});
            skArc(sketch, "E23.93.3", {"start": v(7.21, 15.32) * mm, "mid": v(8.3, 16.1) * mm, "end": v(9.1, 17.18) * mm});
            skLineSegment(sketch, "E23.93.4", {"start": v(5.73, 13.22) * mm, "end": v(5.22, 13.46) * mm});
            skLineSegment(sketch, "E23.93.5", {"start": v(8.58, 17.42) * mm, "end": v(9.1, 17.18) * mm});
            skArc(sketch, "E23.94.0", {"start": v(4.36, 13.76) * mm, "mid": v(5.16, 14.78) * mm, "end": v(5.68, 15.96) * mm});
            skArc(sketch, "E23.94.1", {"start": v(5.68, 15.96) * mm, "mid": v(6.7, 16.82) * mm, "end": v(7.47, 17.93) * mm});
            skArc(sketch, "E23.94.2", {"start": v(4.89, 13.55) * mm, "mid": v(5.66, 14.6) * mm, "end": v(6.23, 15.75) * mm});
            skArc(sketch, "E23.94.3", {"start": v(6.23, 15.75) * mm, "mid": v(7.28, 16.58) * mm, "end": v(8, 17.72) * mm});
            skLineSegment(sketch, "E23.94.4", {"start": v(4.89, 13.55) * mm, "end": v(4.36, 13.76) * mm});
            skLineSegment(sketch, "E23.94.5", {"start": v(7.47, 17.93) * mm, "end": v(8, 17.72) * mm});
            skArc(sketch, "E23.95.0", {"start": v(3.49, 14) * mm, "mid": v(4.23, 15.07) * mm, "end": v(4.67, 16.29) * mm});
            skArc(sketch, "E23.95.1", {"start": v(4.67, 16.29) * mm, "mid": v(5.64, 17.21) * mm, "end": v(6.33, 18.36) * mm});
            skArc(sketch, "E23.95.2", {"start": v(4.03, 13.84) * mm, "mid": v(4.73, 14.92) * mm, "end": v(5.23, 16.1) * mm});
            skArc(sketch, "E23.95.3", {"start": v(5.23, 16.1) * mm, "mid": v(6.23, 17) * mm, "end": v(6.87, 18.18) * mm});
            skLineSegment(sketch, "E23.95.4", {"start": v(4.03, 13.84) * mm, "end": v(3.49, 14) * mm});
            skLineSegment(sketch, "E23.95.5", {"start": v(6.33, 18.36) * mm, "end": v(6.87, 18.18) * mm});
            skArc(sketch, "E23.96.0", {"start": v(2.6, 14.2) * mm, "mid": v(3.27, 15.3) * mm, "end": v(3.64, 16.55) * mm});
            skArc(sketch, "E23.96.1", {"start": v(3.64, 16.55) * mm, "mid": v(4.55, 17.53) * mm, "end": v(5.16, 18.72) * mm});
            skArc(sketch, "E23.96.2", {"start": v(3.15, 14.06) * mm, "mid": v(3.78, 15.19) * mm, "end": v(4.21, 16.4) * mm});
            skArc(sketch, "E23.96.3", {"start": v(4.21, 16.4) * mm, "mid": v(5.15, 17.36) * mm, "end": v(5.71, 18.58) * mm});
            skLineSegment(sketch, "E23.96.4", {"start": v(3.15, 14.06) * mm, "end": v(2.6, 14.2) * mm});
            skLineSegment(sketch, "E23.96.5", {"start": v(5.16, 18.72) * mm, "end": v(5.71, 18.58) * mm});
            skArc(sketch, "E23.97.0", {"start": v(1.7, 14.34) * mm, "mid": v(2.3, 15.48) * mm, "end": v(2.59, 16.75) * mm});
            skArc(sketch, "E23.97.1", {"start": v(2.59, 16.75) * mm, "mid": v(3.44, 17.78) * mm, "end": v(3.98, 19) * mm});
            skArc(sketch, "E23.97.2", {"start": v(2.26, 14.23) * mm, "mid": v(2.82, 15.4) * mm, "end": v(3.17, 16.64) * mm});
            skArc(sketch, "E23.97.3", {"start": v(3.17, 16.64) * mm, "mid": v(4.05, 17.65) * mm, "end": v(4.53, 18.9) * mm});
            skLineSegment(sketch, "E23.97.4", {"start": v(2.26, 14.23) * mm, "end": v(1.7, 14.34) * mm});
            skLineSegment(sketch, "E23.97.5", {"start": v(3.98, 19) * mm, "end": v(4.53, 18.9) * mm});
            skArc(sketch, "E23.98.0", {"start": v(0.8, 14.42) * mm, "mid": v(1.33, 15.6) * mm, "end": v(1.53, 16.88) * mm});
            skArc(sketch, "E23.98.1", {"start": v(1.53, 16.88) * mm, "mid": v(2.31, 17.96) * mm, "end": v(2.78, 19.22) * mm});
            skArc(sketch, "E23.98.2", {"start": v(1.36, 14.34) * mm, "mid": v(1.85, 15.54) * mm, "end": v(2.12, 16.8) * mm});
            skArc(sketch, "E23.98.3", {"start": v(2.12, 16.8) * mm, "mid": v(2.93, 17.87) * mm, "end": v(3.34, 19.15) * mm});
            skLineSegment(sketch, "E23.98.4", {"start": v(1.36, 14.34) * mm, "end": v(0.8, 14.42) * mm});
            skLineSegment(sketch, "E23.98.5", {"start": v(2.78, 19.22) * mm, "end": v(3.34, 19.15) * mm});
            skArc(sketch, "E23.99.0", {"start": v(-0.1, 14.44) * mm, "mid": v(0.35, 15.65) * mm, "end": v(0.47, 16.94) * mm});
            skArc(sketch, "E23.99.1", {"start": v(0.47, 16.94) * mm, "mid": v(1.18, 18.07) * mm, "end": v(1.56, 19.36) * mm});
            skArc(sketch, "E23.99.2", {"start": v(0.46, 14.4) * mm, "mid": v(0.87, 15.63) * mm, "end": v(1.06, 16.9) * mm});
            skArc(sketch, "E23.99.3", {"start": v(1.06, 16.9) * mm, "mid": v(1.8, 18.02) * mm, "end": v(2.13, 19.32) * mm});
            skLineSegment(sketch, "E23.99.4", {"start": v(0.46, 14.4) * mm, "end": v(-0.1, 14.44) * mm});
            skLineSegment(sketch, "E23.99.5", {"start": v(1.56, 19.36) * mm, "end": v(2.13, 19.32) * mm});
            skPoint(sketch, "E23.center", {"position": v(0, 0) * mm});
            skSolve(sketch);
        }
        {
            var Q0;
            Q0=qSketchRegion(id+"F8",true);
            extrude(context, id + "F9", {"entities" : qUnion([Q0]), "operationType" : NewBodyOperationType.ADD, "depth" : 10 * mm});
        }
    });
